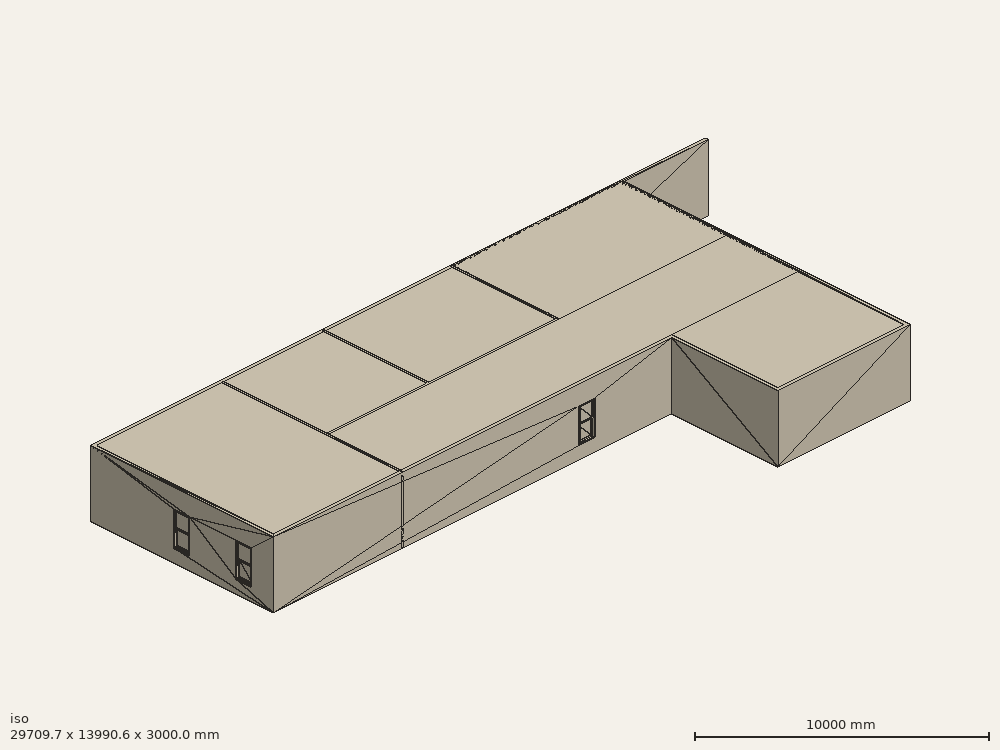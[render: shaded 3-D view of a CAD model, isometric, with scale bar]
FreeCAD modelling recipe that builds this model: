
FCSTD DOCUMENT  (FreeCAD 1.1R39750 (Git))
Label: sm8propc
License: All rights reserved
objects: Part::FeaturePython×23, Sketcher::SketchObject×19, App::DocumentObjectGroup×5, App::GeometryPython×2, Part::Part2DObjectPython×1, App::FeaturePython×1, Spreadsheet::Sheet×1
note: 64 computed .brp shape members not serialized (recipe doc carries the construction recipe); baked Part::Feature solids carry a one-line shape summary decoded from their .brp

FEATURE [Part::Part2DObjectPython] Rectangle  label="Building Outline"  # Draft 2D object (typed FeaturePython)
  Area = 0
  ChamferSize = 0
  Columns = 1
  FilletRadius = 0
  Height = 24384
  Length = 30480
  MakeFace = false
  Rows = 1
FEATURE [App::FeaturePython] Text  label="Building Label"  # WARN: FeaturePython — macro-defined, semantics opaque (R4)
  Placement = pos=(60.96,-290.576,0) rot=(0,0,1;0rad)
  Text =  Building
FEATURE [Sketcher::SketchObject] Sketch
  ArcFitTolerance = 1e-06
  ExternalTypes = [0]
  FullyConstrained = false
  MakeInternals = false
  sketch-geometry (6):
    g0: LineSegment StartX=1970.5 StartY=20576.5 StartZ=0 EndX=27570.1 EndY=20576.5 EndZ=0
    g1: LineSegment StartX=27570.1 StartY=20576.5 StartZ=0 EndX=27570.1 EndY=6625.89 EndZ=0
    g2: LineSegment StartX=27570.1 StartY=6625.89 StartZ=0 EndX=21181.9 EndY=6625.89 EndZ=0
    g3: LineSegment StartX=21181.9 StartY=6625.89 StartZ=0 EndX=21181.9 EndY=11745.8 EndZ=0
    g4: LineSegment StartX=21181.9 StartY=11745.8 StartZ=0 EndX=1970.5 EndY=11745.8 EndZ=0
    g5: LineSegment StartX=1970.5 StartY=11745.8 StartZ=0 EndX=1970.5 EndY=20576.5 EndZ=0
  constraints (12):
    c: Horizontal(g0)
    c: Coincident(g0,g1)
    c: Vertical(g1)
    c: Coincident(g1,g2)
    c: Horizontal(g2)
    c: Coincident(g2,g3)
    c: Vertical(g3)
    c: Coincident(g3,g4)
    c: Horizontal(g4)
    c: Coincident(g4,g5)
    c: Coincident(g5,g0)
    c: Vertical(g5)
FEATURE [App::DocumentObjectGroup] App__DocumentObjectGroup  label="Building Layout"
  Group = -> [Rectangle,Sketch,Text]
FEATURE [App::DocumentObjectGroup] Group001  label="Floors"
FEATURE [Sketcher::SketchObject] Sketch001
  ArcFitTolerance = 1e-06
  ExternalGeometry = -> [Sketch]
  ExternalTypes = [0]
  FullyConstrained = false
  MakeInternals = false
  sketch-geometry (6):
    g0: LineSegment StartX=27570.1 StartY=20576.5 StartZ=0 EndX=27570.1 EndY=6625.89 EndZ=0
    g1: LineSegment StartX=27570.1 StartY=6625.89 StartZ=0 EndX=21181.9 EndY=6625.89 EndZ=0
    g2: LineSegment StartX=21181.9 StartY=6625.89 StartZ=0 EndX=21181.9 EndY=11745.8 EndZ=0
    g3: LineSegment StartX=21181.9 StartY=11745.8 StartZ=0 EndX=1970.5 EndY=11745.8 EndZ=0
    g4: LineSegment StartX=1970.5 StartY=11745.8 StartZ=0 EndX=1970.5 EndY=20576.5 EndZ=0
    g5: LineSegment StartX=1970.5 StartY=20576.5 StartZ=0 EndX=23456.9 EndY=20576.5 EndZ=0
  constraints (10):
    c: Coincident(g0,g-5)
    c: Coincident(g0,g1)
    c: Coincident(g1,g-4)
    c: Coincident(g1,g2)
    c: Coincident(g2,g-4)
    c: Coincident(g2,g3)
    c: Coincident(g3,g-3)
    c: Coincident(g3,g4)
    c: Coincident(g5,g4)
    c: Horizontal(g5)
FEATURE [Part::FeaturePython] Wall  # Arch/BIM 166 (typed FeaturePython)
  Align = 0
  ArchSketchData = true
  ArchSketchPropertySet = 0
  Area = 2.2359e+08
  Base = -> Sketch001
  BlockHeight = 0
  BlockLength = 0
  CountBroken = 0
  CountEntire = 0
  Face = 0
  GlobalId = 2YRsmEokzAbB9aqL5j59_R
  Height = 3000
  HorizontalArea = 0
  IfcData = IfcUID=2YRsmEokzAbB9aqL5j59_R,+2 more (map truncated)
  IfcProperties = AcousticRating;;Pset_WallCommon=IfcLabel;;,Combustible;;Pset_WallCommon=IfcBoolean;;,Compartmentation;;Pset_WallCommon=IfcBoolean;;,+7 more (map truncated)
  IfcType = 166
  Joint = 0
  Length = 74529.9
  MakeBlocks = false
  MoveBase = false
  MoveWithHost = false
  Normal = (0,0,0)
  OffsetFirst = 0
  OffsetSecond = 0
  PerimeterLength = 0
  PredefinedType = 0
  VerticalArea = 0
  Width = 152.4
FEATURE [Sketcher::SketchObject] Sketch002
  ArcFitTolerance = 1e-06
  ExternalGeometry = -> [Sketch]
  ExternalTypes = [0]
  FullyConstrained = false
  MakeInternals = false
  sketch-geometry (6):
    g0: LineSegment StartX=19340.5 StartY=20576.5 StartZ=0 EndX=19340.5 EndY=15418.3 EndZ=0
    g1: LineSegment StartX=19340.5 StartY=15418.3 StartZ=0 EndX=13139 EndY=15418.3 EndZ=0
    g2: LineSegment StartX=13139 StartY=15418.3 StartZ=0 EndX=13139 EndY=20576.5 EndZ=0
    g3: LineSegment StartX=13139 StartY=15418.3 StartZ=0 EndX=8206.95 EndY=15418.3 EndZ=0
    g4: LineSegment StartX=8206.95 StartY=15418.3 StartZ=0 EndX=8206.95 EndY=20576.5 EndZ=0
    g5: LineSegment StartX=8206.95 StartY=15418.3 StartZ=0 EndX=8206.95 EndY=11745.8 EndZ=0
  constraints (16):
    c: PointOnObject(g0,g-3)
    c: Vertical(g0)
    c: Coincident(g0,g1)
    c: Horizontal(g1)
    c: Coincident(g1,g2)
    c: PointOnObject(g2,g-3)
    c: Vertical(g2)
    c: Coincident(g1,g3)
    c: Horizontal(g3)
    c: Coincident(g3,g4)
    c: PointOnObject(g4,g-3)
    c: Vertical(g4)
    c: Coincident(g3,g5)
    c: Vertical(g5)
    c: DistanceY(g5,g-4) = 0
    c: DistanceX(g0,g-3) = 8229.6
FEATURE [Part::FeaturePython] Wall001  # Arch/BIM 166 (typed FeaturePython)
  Align = 2
  ArchSketchData = true
  ArchSketchPropertySet = 0
  Area = 9.08412e+07
  Base = -> Sketch002
  BlockHeight = 0
  BlockLength = 0
  CountBroken = 0
  CountEntire = 0
  Face = 0
  GlobalId = 1JO$GA0_55Qeh9h4$oH2jA
  Height = 3000
  HorizontalArea = 0
  IfcData = IfcUID=1JO$GA0_55Qeh9h4$oH2jA,+2 more (map truncated)
  IfcType = 166
  Joint = 0
  Length = 30280.4
  MakeBlocks = false
  MoveBase = false
  MoveWithHost = false
  Normal = (0,0,0)
  OffsetFirst = 0
  OffsetSecond = 0
  PerimeterLength = 0
  PredefinedType = 0
  VerticalArea = 0
  Width = 101.6
FEATURE [Sketcher::SketchObject] Sketch003
  ArcFitTolerance = 1e-06
  ExternalTypes = [0]
  FullyConstrained = true
  MakeInternals = false
  Placement = pos=(27570.1,8934.96,609.6) rot=(0.57735,0.57735,0.57735;2.0944rad)
  sketch-geometry (24):
    g0: LineSegment StartX=0 StartY=0 StartZ=0 EndX=762 EndY=0 EndZ=0
    g1: LineSegment StartX=762 StartY=0 StartZ=0 EndX=762 EndY=1524 EndZ=0
    g2: LineSegment StartX=762 StartY=1524 StartZ=0 EndX=0 EndY=1524 EndZ=0
    g3: LineSegment StartX=0 StartY=1524 StartZ=0 EndX=0 EndY=0 EndZ=0
    g4: LineSegment StartX=25 StartY=25 StartZ=0 EndX=737 EndY=25 EndZ=0
    g5: LineSegment StartX=737 StartY=25 StartZ=0 EndX=737 EndY=1499 EndZ=0
    g6: LineSegment StartX=737 StartY=1499 StartZ=0 EndX=25 EndY=1499 EndZ=0
    g7: LineSegment StartX=25 StartY=1499 StartZ=0 EndX=25 EndY=25 EndZ=0
    g8: LineSegment StartX=27.5 StartY=27.5 StartZ=0 EndX=734.5 EndY=27.5 EndZ=0
    g9: LineSegment StartX=734.5 StartY=27.5 StartZ=0 EndX=734.5 EndY=760.75 EndZ=0
    g10: LineSegment StartX=734.5 StartY=760.75 StartZ=0 EndX=27.5 EndY=760.75 EndZ=0
    g11: LineSegment StartX=27.5 StartY=760.75 StartZ=0 EndX=27.5 EndY=27.5 EndZ=0
    g12: LineSegment StartX=77.5 StartY=77.5 StartZ=0 EndX=684.5 EndY=77.5 EndZ=0
    g13: LineSegment StartX=684.5 StartY=77.5 StartZ=0 EndX=684.5 EndY=710.75 EndZ=0
    g14: LineSegment StartX=684.5 StartY=710.75 StartZ=0 EndX=77.5 EndY=710.75 EndZ=0
    g15: LineSegment StartX=77.5 StartY=710.75 StartZ=0 EndX=77.5 EndY=77.5 EndZ=0
    g16: LineSegment StartX=27.5 StartY=763.25 StartZ=0 EndX=734.5 EndY=763.25 EndZ=0
    g17: LineSegment StartX=734.5 StartY=763.25 StartZ=0 EndX=734.5 EndY=1496.5 EndZ=0
    g18: LineSegment StartX=734.5 StartY=1496.5 StartZ=0 EndX=27.5 EndY=1496.5 EndZ=0
    g19: LineSegment StartX=27.5 StartY=1496.5 StartZ=0 EndX=27.5 EndY=763.25 EndZ=0
    g20: LineSegment StartX=77.5 StartY=813.25 StartZ=0 EndX=684.5 EndY=813.25 EndZ=0
    g21: LineSegment StartX=684.5 StartY=813.25 StartZ=0 EndX=684.5 EndY=1446.5 EndZ=0
    g22: LineSegment StartX=684.5 StartY=1446.5 StartZ=0 EndX=77.5 EndY=1446.5 EndZ=0
    g23: LineSegment StartX=77.5 StartY=1446.5 StartZ=0 EndX=77.5 EndY=813.25 EndZ=0
  constraints (71):
    c: Coincident(g0,g1)
    c: Coincident(g1,g2)
    c: Coincident(g2,g3)
    c: Coincident(g3,g0)
    c: Horizontal(g0)
    c: Horizontal(g2)
    c: Vertical(g1)
    c: Vertical(g3)
    c: Coincident(g4,g5)
    c: Coincident(g5,g6)
    c: Coincident(g6,g7)
    c: Coincident(g7,g4)
    c: Horizontal(g4)
    c: Horizontal(g6)
    c: Vertical(g5)
    c: Vertical(g7)
    c: DistanceY(g1) = 1524  'Height'
    c: DistanceX(g0) = 762  'Width'
    c: DistanceY(g6,g2) = 25  'Frame1'
    c: DistanceX(g2,g6) = 25  'Frame2'
    c: DistanceX(g4,g0) = 25  'Frame3'
    c: DistanceY(g0,g4) = 25  'Frame4'
    c: Coincident(g0,g-1)
    c: Coincident(g8,g9)
    c: Coincident(g9,g10)
    c: Coincident(g10,g11)
    c: Coincident(g11,g8)
    c: Horizontal(g8)
    c: Horizontal(g10)
    c: Vertical(g9)
    c: Vertical(g11)
    c: Coincident(g12,g13)
    c: Coincident(g13,g14)
    c: Coincident(g14,g15)
    c: Coincident(g15,g12)
    c: Horizontal(g12)
    c: Horizontal(g14)
    c: Vertical(g13)
    c: Vertical(g15)
    c: Coincident(g16,g17)
    c: Coincident(g17,g18)
    c: Coincident(g18,g19)
    c: Coincident(g19,g16)
    c: Horizontal(g16)
    c: Horizontal(g18)
    c: Vertical(g17)
    c: Vertical(g19)
    c: Coincident(g20,g21)
    c: Coincident(g21,g22)
    c: Coincident(g22,g23)
    c: Coincident(g23,g20)
    c: Horizontal(g20)
    c: Horizontal(g22)
    c: Vertical(g21)
    c: Vertical(g23)
    c: DistanceY(g8,g12) = 50
    c: DistanceX(g8,g12) = 50
    c: DistanceX(g21,g17) = 50
    c: DistanceY(g21,g17) = 50
    c: DistanceY(g16,g20) = 50
    c: DistanceY(g10,g14) = -50
    c: Equal(g23,g15)
    c: DistanceX(g12,g20) = 0
    c: DistanceX(g13,g20) = 0
    c: DistanceX(g4,g8) = 2.5
    c: DistanceY(g4,g8) = 2.5
    c: DistanceX(g6,g18) = -2.5
    c: DistanceY(g6,g18) = -2.5
    c: DistanceY(g10,g16) = 2.5
    c: PointOnObject(g9,g17)
    c: PointOnObject(g16,g11)
FEATURE [Part::FeaturePython] Window  # Arch/BIM 170 (typed FeaturePython)
  Area = 1161288
  Base = -> Sketch003
  Frame = 50.8
  GlobalId = 2kA35zzJj5FhV35RYvWuJY
  Height = 1524
  HoleDepth = 0
  HoleWire = 0
  HorizontalArea = 0
  Hosts = -> [Wall]
  IfcData = IfcUID=2kA35zzJj5FhV35RYvWuJY,+2 more (map truncated)
  IfcType = 170
  LouvreSpacing = 0
  LouvreWidth = 0
  MoveBase = false
  MoveWithHost = true
  Normal = (-1,0,0)
  Opening = 0
  OverallHeight = 1524
  OverallWidth = 762
  PartitioningType = 0
  PerimeterLength = 0
  PredefinedType = 0
  Preset = 4
  SymbolElevation = false
  SymbolPlan = false
  VerticalArea = 0
  Width = 762
  WindowParts = OuterFrame | Frame | Wire0,Wire1 | -90.8+V | 0.00+V | LowerFrame | Frame | Wire2,Wire3 | 50.8 | 75.8+V | LowerGlass | Glass panel | Wire3 | 5.08 | 101.19999999999999+V | UpperFrame | Frame | Wire4,Wire5 | 50.8 | 25.0+V | UpperGlass | Glass panel | Wire5 | 5.08 | 50.4+V
  expr: OverallHeight = .Height.Value
  expr: OverallWidth = .Width.Value
FEATURE [Sketcher::SketchObject] Sketch004
  ArcFitTolerance = 1e-06
  ExternalTypes = [0]
  FullyConstrained = true
  MakeInternals = false
  Placement = pos=(27570.1,18031.7,609.6) rot=(0.57735,0.57735,0.57735;2.0944rad)
  sketch-geometry (24):
    g0: LineSegment StartX=0 StartY=0 StartZ=0 EndX=762 EndY=0 EndZ=0
    g1: LineSegment StartX=762 StartY=0 StartZ=0 EndX=762 EndY=1524 EndZ=0
    g2: LineSegment StartX=762 StartY=1524 StartZ=0 EndX=0 EndY=1524 EndZ=0
    g3: LineSegment StartX=0 StartY=1524 StartZ=0 EndX=0 EndY=0 EndZ=0
    g4: LineSegment StartX=25 StartY=25 StartZ=0 EndX=737 EndY=25 EndZ=0
    g5: LineSegment StartX=737 StartY=25 StartZ=0 EndX=737 EndY=1499 EndZ=0
    g6: LineSegment StartX=737 StartY=1499 StartZ=0 EndX=25 EndY=1499 EndZ=0
    g7: LineSegment StartX=25 StartY=1499 StartZ=0 EndX=25 EndY=25 EndZ=0
    g8: LineSegment StartX=27.5 StartY=27.5 StartZ=0 EndX=734.5 EndY=27.5 EndZ=0
    g9: LineSegment StartX=734.5 StartY=27.5 StartZ=0 EndX=734.5 EndY=760.75 EndZ=0
    g10: LineSegment StartX=734.5 StartY=760.75 StartZ=0 EndX=27.5 EndY=760.75 EndZ=0
    g11: LineSegment StartX=27.5 StartY=760.75 StartZ=0 EndX=27.5 EndY=27.5 EndZ=0
    g12: LineSegment StartX=77.5 StartY=77.5 StartZ=0 EndX=684.5 EndY=77.5 EndZ=0
    g13: LineSegment StartX=684.5 StartY=77.5 StartZ=0 EndX=684.5 EndY=710.75 EndZ=0
    g14: LineSegment StartX=684.5 StartY=710.75 StartZ=0 EndX=77.5 EndY=710.75 EndZ=0
    g15: LineSegment StartX=77.5 StartY=710.75 StartZ=0 EndX=77.5 EndY=77.5 EndZ=0
    g16: LineSegment StartX=27.5 StartY=763.25 StartZ=0 EndX=734.5 EndY=763.25 EndZ=0
    g17: LineSegment StartX=734.5 StartY=763.25 StartZ=0 EndX=734.5 EndY=1496.5 EndZ=0
    g18: LineSegment StartX=734.5 StartY=1496.5 StartZ=0 EndX=27.5 EndY=1496.5 EndZ=0
    g19: LineSegment StartX=27.5 StartY=1496.5 StartZ=0 EndX=27.5 EndY=763.25 EndZ=0
    g20: LineSegment StartX=77.5 StartY=813.25 StartZ=0 EndX=684.5 EndY=813.25 EndZ=0
    g21: LineSegment StartX=684.5 StartY=813.25 StartZ=0 EndX=684.5 EndY=1446.5 EndZ=0
    g22: LineSegment StartX=684.5 StartY=1446.5 StartZ=0 EndX=77.5 EndY=1446.5 EndZ=0
    g23: LineSegment StartX=77.5 StartY=1446.5 StartZ=0 EndX=77.5 EndY=813.25 EndZ=0
  constraints (71):
    c: Coincident(g0,g1)
    c: Coincident(g1,g2)
    c: Coincident(g2,g3)
    c: Coincident(g3,g0)
    c: Horizontal(g0)
    c: Horizontal(g2)
    c: Vertical(g1)
    c: Vertical(g3)
    c: Coincident(g4,g5)
    c: Coincident(g5,g6)
    c: Coincident(g6,g7)
    c: Coincident(g7,g4)
    c: Horizontal(g4)
    c: Horizontal(g6)
    c: Vertical(g5)
    c: Vertical(g7)
    c: DistanceY(g1) = 1524  'Height'
    c: DistanceX(g0) = 762  'Width'
    c: DistanceY(g6,g2) = 25  'Frame1'
    c: DistanceX(g2,g6) = 25  'Frame2'
    c: DistanceX(g4,g0) = 25  'Frame3'
    c: DistanceY(g0,g4) = 25  'Frame4'
    c: Coincident(g0,g-1)
    c: Coincident(g8,g9)
    c: Coincident(g9,g10)
    c: Coincident(g10,g11)
    c: Coincident(g11,g8)
    c: Horizontal(g8)
    c: Horizontal(g10)
    c: Vertical(g9)
    c: Vertical(g11)
    c: Coincident(g12,g13)
    c: Coincident(g13,g14)
    c: Coincident(g14,g15)
    c: Coincident(g15,g12)
    c: Horizontal(g12)
    c: Horizontal(g14)
    c: Vertical(g13)
    c: Vertical(g15)
    c: Coincident(g16,g17)
    c: Coincident(g17,g18)
    c: Coincident(g18,g19)
    c: Coincident(g19,g16)
    c: Horizontal(g16)
    c: Horizontal(g18)
    c: Vertical(g17)
    c: Vertical(g19)
    c: Coincident(g20,g21)
    c: Coincident(g21,g22)
    c: Coincident(g22,g23)
    c: Coincident(g23,g20)
    c: Horizontal(g20)
    c: Horizontal(g22)
    c: Vertical(g21)
    c: Vertical(g23)
    c: DistanceY(g8,g12) = 50
    c: DistanceX(g8,g12) = 50
    c: DistanceX(g21,g17) = 50
    c: DistanceY(g21,g17) = 50
    c: DistanceY(g16,g20) = 50
    c: DistanceY(g10,g14) = -50
    c: Equal(g23,g15)
    c: DistanceX(g12,g20) = 0
    c: DistanceX(g13,g20) = 0
    c: DistanceX(g4,g8) = 2.5
    c: DistanceY(g4,g8) = 2.5
    c: DistanceX(g6,g18) = -2.5
    c: DistanceY(g6,g18) = -2.5
    c: DistanceY(g10,g16) = 2.5
    c: PointOnObject(g9,g17)
    c: PointOnObject(g16,g11)
FEATURE [Part::FeaturePython] Window001  # Arch/BIM 170 (typed FeaturePython)
  Area = 1161288
  Base = -> Sketch004
  Frame = 50.8
  GlobalId = 0Gm0yBXcz24Rl4COUdGdtV
  Height = 1524
  HoleDepth = 0
  HoleWire = 0
  HorizontalArea = 0
  Hosts = -> [Wall]
  IfcData = IfcUID=0Gm0yBXcz24Rl4COUdGdtV,+2 more (map truncated)
  IfcType = 170
  LouvreSpacing = 0
  LouvreWidth = 0
  MoveBase = false
  MoveWithHost = true
  Normal = (-1,0,0)
  Opening = 0
  OverallHeight = 1524
  OverallWidth = 762
  PartitioningType = 0
  PerimeterLength = 0
  PredefinedType = 0
  Preset = 4
  SymbolElevation = false
  SymbolPlan = false
  VerticalArea = 0
  Width = 762
  WindowParts = <same value as first occurrence — deduplicated (x10 in doc)>
  expr: OverallHeight = .Height.Value
  expr: OverallWidth = .Width.Value
FEATURE [Sketcher::SketchObject] Sketch005
  ArcFitTolerance = 1e-06
  ExternalTypes = [0]
  FullyConstrained = true
  MakeInternals = false
  Placement = pos=(21499.9,20576.5,611.457) rot=(0,0.707107,0.707107;3.14159rad)
  sketch-geometry (24):
    g0: LineSegment StartX=0 StartY=0 StartZ=0 EndX=762 EndY=0 EndZ=0
    g1: LineSegment StartX=762 StartY=0 StartZ=0 EndX=762 EndY=1524 EndZ=0
    g2: LineSegment StartX=762 StartY=1524 StartZ=0 EndX=0 EndY=1524 EndZ=0
    g3: LineSegment StartX=0 StartY=1524 StartZ=0 EndX=0 EndY=0 EndZ=0
    g4: LineSegment StartX=25 StartY=25 StartZ=0 EndX=737 EndY=25 EndZ=0
    g5: LineSegment StartX=737 StartY=25 StartZ=0 EndX=737 EndY=1499 EndZ=0
    g6: LineSegment StartX=737 StartY=1499 StartZ=0 EndX=25 EndY=1499 EndZ=0
    g7: LineSegment StartX=25 StartY=1499 StartZ=0 EndX=25 EndY=25 EndZ=0
    g8: LineSegment StartX=27.5 StartY=27.5 StartZ=0 EndX=734.5 EndY=27.5 EndZ=0
    g9: LineSegment StartX=734.5 StartY=27.5 StartZ=0 EndX=734.5 EndY=760.75 EndZ=0
    g10: LineSegment StartX=734.5 StartY=760.75 StartZ=0 EndX=27.5 EndY=760.75 EndZ=0
    g11: LineSegment StartX=27.5 StartY=760.75 StartZ=0 EndX=27.5 EndY=27.5 EndZ=0
    g12: LineSegment StartX=77.5 StartY=77.5 StartZ=0 EndX=684.5 EndY=77.5 EndZ=0
    g13: LineSegment StartX=684.5 StartY=77.5 StartZ=0 EndX=684.5 EndY=710.75 EndZ=0
    g14: LineSegment StartX=684.5 StartY=710.75 StartZ=0 EndX=77.5 EndY=710.75 EndZ=0
    g15: LineSegment StartX=77.5 StartY=710.75 StartZ=0 EndX=77.5 EndY=77.5 EndZ=0
    g16: LineSegment StartX=27.5 StartY=763.25 StartZ=0 EndX=734.5 EndY=763.25 EndZ=0
    g17: LineSegment StartX=734.5 StartY=763.25 StartZ=0 EndX=734.5 EndY=1496.5 EndZ=0
    g18: LineSegment StartX=734.5 StartY=1496.5 StartZ=0 EndX=27.5 EndY=1496.5 EndZ=0
    g19: LineSegment StartX=27.5 StartY=1496.5 StartZ=0 EndX=27.5 EndY=763.25 EndZ=0
    g20: LineSegment StartX=77.5 StartY=813.25 StartZ=0 EndX=684.5 EndY=813.25 EndZ=0
    g21: LineSegment StartX=684.5 StartY=813.25 StartZ=0 EndX=684.5 EndY=1446.5 EndZ=0
    g22: LineSegment StartX=684.5 StartY=1446.5 StartZ=0 EndX=77.5 EndY=1446.5 EndZ=0
    g23: LineSegment StartX=77.5 StartY=1446.5 StartZ=0 EndX=77.5 EndY=813.25 EndZ=0
  constraints (71):
    c: Coincident(g0,g1)
    c: Coincident(g1,g2)
    c: Coincident(g2,g3)
    c: Coincident(g3,g0)
    c: Horizontal(g0)
    c: Horizontal(g2)
    c: Vertical(g1)
    c: Vertical(g3)
    c: Coincident(g4,g5)
    c: Coincident(g5,g6)
    c: Coincident(g6,g7)
    c: Coincident(g7,g4)
    c: Horizontal(g4)
    c: Horizontal(g6)
    c: Vertical(g5)
    c: Vertical(g7)
    c: DistanceY(g1) = 1524  'Height'
    c: DistanceX(g0) = 762  'Width'
    c: DistanceY(g6,g2) = 25  'Frame1'
    c: DistanceX(g2,g6) = 25  'Frame2'
    c: DistanceX(g4,g0) = 25  'Frame3'
    c: DistanceY(g0,g4) = 25  'Frame4'
    c: Coincident(g0,g-1)
    c: Coincident(g8,g9)
    c: Coincident(g9,g10)
    c: Coincident(g10,g11)
    c: Coincident(g11,g8)
    c: Horizontal(g8)
    c: Horizontal(g10)
    c: Vertical(g9)
    c: Vertical(g11)
    c: Coincident(g12,g13)
    c: Coincident(g13,g14)
    c: Coincident(g14,g15)
    c: Coincident(g15,g12)
    c: Horizontal(g12)
    c: Horizontal(g14)
    c: Vertical(g13)
    c: Vertical(g15)
    c: Coincident(g16,g17)
    c: Coincident(g17,g18)
    c: Coincident(g18,g19)
    c: Coincident(g19,g16)
    c: Horizontal(g16)
    c: Horizontal(g18)
    c: Vertical(g17)
    c: Vertical(g19)
    c: Coincident(g20,g21)
    c: Coincident(g21,g22)
    c: Coincident(g22,g23)
    c: Coincident(g23,g20)
    c: Horizontal(g20)
    c: Horizontal(g22)
    c: Vertical(g21)
    c: Vertical(g23)
    c: DistanceY(g8,g12) = 50
    c: DistanceX(g8,g12) = 50
    c: DistanceX(g21,g17) = 50
    c: DistanceY(g21,g17) = 50
    c: DistanceY(g16,g20) = 50
    c: DistanceY(g10,g14) = -50
    c: Equal(g23,g15)
    c: DistanceX(g12,g20) = 0
    c: DistanceX(g13,g20) = 0
    c: DistanceX(g4,g8) = 2.5
    c: DistanceY(g4,g8) = 2.5
    c: DistanceX(g6,g18) = -2.5
    c: DistanceY(g6,g18) = -2.5
    c: DistanceY(g10,g16) = 2.5
    c: PointOnObject(g9,g17)
    c: PointOnObject(g16,g11)
FEATURE [Part::FeaturePython] Window002  # Arch/BIM 170 (typed FeaturePython)
  Area = 1161288
  Base = -> Sketch005
  Frame = 50.8
  GlobalId = 1_nrbuonLC$gQXA2knc8Ya
  Height = 1524
  HoleDepth = 0
  HoleWire = 0
  HorizontalArea = 0
  Hosts = -> [Wall]
  IfcData = IfcUID=1_nrbuonLC$gQXA2knc8Ya,+2 more (map truncated)
  IfcType = 170
  LouvreSpacing = 0
  LouvreWidth = 0
  MoveBase = false
  MoveWithHost = true
  Normal = (0,-1,2e-16)
  Opening = 0
  OverallHeight = 1524
  OverallWidth = 762
  PartitioningType = 0
  PerimeterLength = 0
  PredefinedType = 0
  Preset = 4
  SymbolElevation = false
  SymbolPlan = false
  VerticalArea = 0
  Width = 762
  WindowParts = <same value as first occurrence — deduplicated (x10 in doc)>
  expr: OverallHeight = .Height.Value
  expr: OverallWidth = .Width.Value
FEATURE [Sketcher::SketchObject] Sketch006
  ArcFitTolerance = 1e-06
  ExternalTypes = [0]
  FullyConstrained = true
  MakeInternals = false
  Placement = pos=(17406.2,20576.5,609.6) rot=(0,0.707107,0.707107;3.14159rad)
  sketch-geometry (24):
    g0: LineSegment StartX=0 StartY=0 StartZ=0 EndX=762 EndY=0 EndZ=0
    g1: LineSegment StartX=762 StartY=0 StartZ=0 EndX=762 EndY=1524 EndZ=0
    g2: LineSegment StartX=762 StartY=1524 StartZ=0 EndX=0 EndY=1524 EndZ=0
    g3: LineSegment StartX=0 StartY=1524 StartZ=0 EndX=0 EndY=0 EndZ=0
    g4: LineSegment StartX=25 StartY=25 StartZ=0 EndX=737 EndY=25 EndZ=0
    g5: LineSegment StartX=737 StartY=25 StartZ=0 EndX=737 EndY=1499 EndZ=0
    g6: LineSegment StartX=737 StartY=1499 StartZ=0 EndX=25 EndY=1499 EndZ=0
    g7: LineSegment StartX=25 StartY=1499 StartZ=0 EndX=25 EndY=25 EndZ=0
    g8: LineSegment StartX=27.5 StartY=27.5 StartZ=0 EndX=734.5 EndY=27.5 EndZ=0
    g9: LineSegment StartX=734.5 StartY=27.5 StartZ=0 EndX=734.5 EndY=760.75 EndZ=0
    g10: LineSegment StartX=734.5 StartY=760.75 StartZ=0 EndX=27.5 EndY=760.75 EndZ=0
    g11: LineSegment StartX=27.5 StartY=760.75 StartZ=0 EndX=27.5 EndY=27.5 EndZ=0
    g12: LineSegment StartX=77.5 StartY=77.5 StartZ=0 EndX=684.5 EndY=77.5 EndZ=0
    g13: LineSegment StartX=684.5 StartY=77.5 StartZ=0 EndX=684.5 EndY=710.75 EndZ=0
    g14: LineSegment StartX=684.5 StartY=710.75 StartZ=0 EndX=77.5 EndY=710.75 EndZ=0
    g15: LineSegment StartX=77.5 StartY=710.75 StartZ=0 EndX=77.5 EndY=77.5 EndZ=0
    g16: LineSegment StartX=27.5 StartY=763.25 StartZ=0 EndX=734.5 EndY=763.25 EndZ=0
    g17: LineSegment StartX=734.5 StartY=763.25 StartZ=0 EndX=734.5 EndY=1496.5 EndZ=0
    g18: LineSegment StartX=734.5 StartY=1496.5 StartZ=0 EndX=27.5 EndY=1496.5 EndZ=0
    g19: LineSegment StartX=27.5 StartY=1496.5 StartZ=0 EndX=27.5 EndY=763.25 EndZ=0
    g20: LineSegment StartX=77.5 StartY=813.25 StartZ=0 EndX=684.5 EndY=813.25 EndZ=0
    g21: LineSegment StartX=684.5 StartY=813.25 StartZ=0 EndX=684.5 EndY=1446.5 EndZ=0
    g22: LineSegment StartX=684.5 StartY=1446.5 StartZ=0 EndX=77.5 EndY=1446.5 EndZ=0
    g23: LineSegment StartX=77.5 StartY=1446.5 StartZ=0 EndX=77.5 EndY=813.25 EndZ=0
  constraints (71):
    c: Coincident(g0,g1)
    c: Coincident(g1,g2)
    c: Coincident(g2,g3)
    c: Coincident(g3,g0)
    c: Horizontal(g0)
    c: Horizontal(g2)
    c: Vertical(g1)
    c: Vertical(g3)
    c: Coincident(g4,g5)
    c: Coincident(g5,g6)
    c: Coincident(g6,g7)
    c: Coincident(g7,g4)
    c: Horizontal(g4)
    c: Horizontal(g6)
    c: Vertical(g5)
    c: Vertical(g7)
    c: DistanceY(g1) = 1524  'Height'
    c: DistanceX(g0) = 762  'Width'
    c: DistanceY(g6,g2) = 25  'Frame1'
    c: DistanceX(g2,g6) = 25  'Frame2'
    c: DistanceX(g4,g0) = 25  'Frame3'
    c: DistanceY(g0,g4) = 25  'Frame4'
    c: Coincident(g0,g-1)
    c: Coincident(g8,g9)
    c: Coincident(g9,g10)
    c: Coincident(g10,g11)
    c: Coincident(g11,g8)
    c: Horizontal(g8)
    c: Horizontal(g10)
    c: Vertical(g9)
    c: Vertical(g11)
    c: Coincident(g12,g13)
    c: Coincident(g13,g14)
    c: Coincident(g14,g15)
    c: Coincident(g15,g12)
    c: Horizontal(g12)
    c: Horizontal(g14)
    c: Vertical(g13)
    c: Vertical(g15)
    c: Coincident(g16,g17)
    c: Coincident(g17,g18)
    c: Coincident(g18,g19)
    c: Coincident(g19,g16)
    c: Horizontal(g16)
    c: Horizontal(g18)
    c: Vertical(g17)
    c: Vertical(g19)
    c: Coincident(g20,g21)
    c: Coincident(g21,g22)
    c: Coincident(g22,g23)
    c: Coincident(g23,g20)
    c: Horizontal(g20)
    c: Horizontal(g22)
    c: Vertical(g21)
    c: Vertical(g23)
    c: DistanceY(g8,g12) = 50
    c: DistanceX(g8,g12) = 50
    c: DistanceX(g21,g17) = 50
    c: DistanceY(g21,g17) = 50
    c: DistanceY(g16,g20) = 50
    c: DistanceY(g10,g14) = -50
    c: Equal(g23,g15)
    c: DistanceX(g12,g20) = 0
    c: DistanceX(g13,g20) = 0
    c: DistanceX(g4,g8) = 2.5
    c: DistanceY(g4,g8) = 2.5
    c: DistanceX(g6,g18) = -2.5
    c: DistanceY(g6,g18) = -2.5
    c: DistanceY(g10,g16) = 2.5
    c: PointOnObject(g9,g17)
    c: PointOnObject(g16,g11)
FEATURE [Part::FeaturePython] Window003  # Arch/BIM 170 (typed FeaturePython)
  Area = 1161288
  Base = -> Sketch006
  Frame = 50.8
  GlobalId = 0bJBue1qL8l8j0EzGdZafv
  Height = 1524
  HoleDepth = 0
  HoleWire = 0
  HorizontalArea = 0
  Hosts = -> [Wall]
  IfcData = IfcUID=0bJBue1qL8l8j0EzGdZafv,+2 more (map truncated)
  IfcType = 170
  LouvreSpacing = 0
  LouvreWidth = 0
  MoveBase = false
  MoveWithHost = true
  Normal = (0,-1,2e-16)
  Opening = 0
  OverallHeight = 1524
  OverallWidth = 762
  PartitioningType = 0
  PerimeterLength = 0
  PredefinedType = 0
  Preset = 4
  SymbolElevation = false
  SymbolPlan = false
  VerticalArea = 0
  Width = 762
  WindowParts = <same value as first occurrence — deduplicated (x10 in doc)>
  expr: OverallHeight = .Height.Value
  expr: OverallWidth = .Width.Value
FEATURE [Sketcher::SketchObject] Sketch007
  ArcFitTolerance = 1e-06
  ExternalTypes = [0]
  FullyConstrained = true
  MakeInternals = false
  Placement = pos=(11820.4,20576.5,609.6) rot=(0,0.707107,0.707107;3.14159rad)
  sketch-geometry (24):
    g0: LineSegment StartX=0 StartY=0 StartZ=0 EndX=762 EndY=0 EndZ=0
    g1: LineSegment StartX=762 StartY=0 StartZ=0 EndX=762 EndY=1524 EndZ=0
    g2: LineSegment StartX=762 StartY=1524 StartZ=0 EndX=0 EndY=1524 EndZ=0
    g3: LineSegment StartX=0 StartY=1524 StartZ=0 EndX=0 EndY=0 EndZ=0
    g4: LineSegment StartX=25 StartY=25 StartZ=0 EndX=737 EndY=25 EndZ=0
    g5: LineSegment StartX=737 StartY=25 StartZ=0 EndX=737 EndY=1499 EndZ=0
    g6: LineSegment StartX=737 StartY=1499 StartZ=0 EndX=25 EndY=1499 EndZ=0
    g7: LineSegment StartX=25 StartY=1499 StartZ=0 EndX=25 EndY=25 EndZ=0
    g8: LineSegment StartX=27.5 StartY=27.5 StartZ=0 EndX=734.5 EndY=27.5 EndZ=0
    g9: LineSegment StartX=734.5 StartY=27.5 StartZ=0 EndX=734.5 EndY=760.75 EndZ=0
    g10: LineSegment StartX=734.5 StartY=760.75 StartZ=0 EndX=27.5 EndY=760.75 EndZ=0
    g11: LineSegment StartX=27.5 StartY=760.75 StartZ=0 EndX=27.5 EndY=27.5 EndZ=0
    g12: LineSegment StartX=77.5 StartY=77.5 StartZ=0 EndX=684.5 EndY=77.5 EndZ=0
    g13: LineSegment StartX=684.5 StartY=77.5 StartZ=0 EndX=684.5 EndY=710.75 EndZ=0
    g14: LineSegment StartX=684.5 StartY=710.75 StartZ=0 EndX=77.5 EndY=710.75 EndZ=0
    g15: LineSegment StartX=77.5 StartY=710.75 StartZ=0 EndX=77.5 EndY=77.5 EndZ=0
    g16: LineSegment StartX=27.5 StartY=763.25 StartZ=0 EndX=734.5 EndY=763.25 EndZ=0
    g17: LineSegment StartX=734.5 StartY=763.25 StartZ=0 EndX=734.5 EndY=1496.5 EndZ=0
    g18: LineSegment StartX=734.5 StartY=1496.5 StartZ=0 EndX=27.5 EndY=1496.5 EndZ=0
    g19: LineSegment StartX=27.5 StartY=1496.5 StartZ=0 EndX=27.5 EndY=763.25 EndZ=0
    g20: LineSegment StartX=77.5 StartY=813.25 StartZ=0 EndX=684.5 EndY=813.25 EndZ=0
    g21: LineSegment StartX=684.5 StartY=813.25 StartZ=0 EndX=684.5 EndY=1446.5 EndZ=0
    g22: LineSegment StartX=684.5 StartY=1446.5 StartZ=0 EndX=77.5 EndY=1446.5 EndZ=0
    g23: LineSegment StartX=77.5 StartY=1446.5 StartZ=0 EndX=77.5 EndY=813.25 EndZ=0
  constraints (71):
    c: Coincident(g0,g1)
    c: Coincident(g1,g2)
    c: Coincident(g2,g3)
    c: Coincident(g3,g0)
    c: Horizontal(g0)
    c: Horizontal(g2)
    c: Vertical(g1)
    c: Vertical(g3)
    c: Coincident(g4,g5)
    c: Coincident(g5,g6)
    c: Coincident(g6,g7)
    c: Coincident(g7,g4)
    c: Horizontal(g4)
    c: Horizontal(g6)
    c: Vertical(g5)
    c: Vertical(g7)
    c: DistanceY(g1) = 1524  'Height'
    c: DistanceX(g0) = 762  'Width'
    c: DistanceY(g6,g2) = 25  'Frame1'
    c: DistanceX(g2,g6) = 25  'Frame2'
    c: DistanceX(g4,g0) = 25  'Frame3'
    c: DistanceY(g0,g4) = 25  'Frame4'
    c: Coincident(g0,g-1)
    c: Coincident(g8,g9)
    c: Coincident(g9,g10)
    c: Coincident(g10,g11)
    c: Coincident(g11,g8)
    c: Horizontal(g8)
    c: Horizontal(g10)
    c: Vertical(g9)
    c: Vertical(g11)
    c: Coincident(g12,g13)
    c: Coincident(g13,g14)
    c: Coincident(g14,g15)
    c: Coincident(g15,g12)
    c: Horizontal(g12)
    c: Horizontal(g14)
    c: Vertical(g13)
    c: Vertical(g15)
    c: Coincident(g16,g17)
    c: Coincident(g17,g18)
    c: Coincident(g18,g19)
    c: Coincident(g19,g16)
    c: Horizontal(g16)
    c: Horizontal(g18)
    c: Vertical(g17)
    c: Vertical(g19)
    c: Coincident(g20,g21)
    c: Coincident(g21,g22)
    c: Coincident(g22,g23)
    c: Coincident(g23,g20)
    c: Horizontal(g20)
    c: Horizontal(g22)
    c: Vertical(g21)
    c: Vertical(g23)
    c: DistanceY(g8,g12) = 50
    c: DistanceX(g8,g12) = 50
    c: DistanceX(g21,g17) = 50
    c: DistanceY(g21,g17) = 50
    c: DistanceY(g16,g20) = 50
    c: DistanceY(g10,g14) = -50
    c: Equal(g23,g15)
    c: DistanceX(g12,g20) = 0
    c: DistanceX(g13,g20) = 0
    c: DistanceX(g4,g8) = 2.5
    c: DistanceY(g4,g8) = 2.5
    c: DistanceX(g6,g18) = -2.5
    c: DistanceY(g6,g18) = -2.5
    c: DistanceY(g10,g16) = 2.5
    c: PointOnObject(g9,g17)
    c: PointOnObject(g16,g11)
FEATURE [Sketcher::SketchObject] Sketch008
  ArcFitTolerance = 1e-06
  ExternalTypes = [0]
  FullyConstrained = true
  MakeInternals = false
  Placement = pos=(4976.2,20576.5,609.6) rot=(0,0.707107,0.707107;3.14159rad)
  sketch-geometry (24):
    g0: LineSegment StartX=0 StartY=0 StartZ=0 EndX=762 EndY=0 EndZ=0
    g1: LineSegment StartX=762 StartY=0 StartZ=0 EndX=762 EndY=1524 EndZ=0
    g2: LineSegment StartX=762 StartY=1524 StartZ=0 EndX=0 EndY=1524 EndZ=0
    g3: LineSegment StartX=0 StartY=1524 StartZ=0 EndX=0 EndY=0 EndZ=0
    g4: LineSegment StartX=25 StartY=25 StartZ=0 EndX=737 EndY=25 EndZ=0
    g5: LineSegment StartX=737 StartY=25 StartZ=0 EndX=737 EndY=1499 EndZ=0
    g6: LineSegment StartX=737 StartY=1499 StartZ=0 EndX=25 EndY=1499 EndZ=0
    g7: LineSegment StartX=25 StartY=1499 StartZ=0 EndX=25 EndY=25 EndZ=0
    g8: LineSegment StartX=27.5 StartY=27.5 StartZ=0 EndX=734.5 EndY=27.5 EndZ=0
    g9: LineSegment StartX=734.5 StartY=27.5 StartZ=0 EndX=734.5 EndY=760.75 EndZ=0
    g10: LineSegment StartX=734.5 StartY=760.75 StartZ=0 EndX=27.5 EndY=760.75 EndZ=0
    g11: LineSegment StartX=27.5 StartY=760.75 StartZ=0 EndX=27.5 EndY=27.5 EndZ=0
    g12: LineSegment StartX=77.5 StartY=77.5 StartZ=0 EndX=684.5 EndY=77.5 EndZ=0
    g13: LineSegment StartX=684.5 StartY=77.5 StartZ=0 EndX=684.5 EndY=710.75 EndZ=0
    g14: LineSegment StartX=684.5 StartY=710.75 StartZ=0 EndX=77.5 EndY=710.75 EndZ=0
    g15: LineSegment StartX=77.5 StartY=710.75 StartZ=0 EndX=77.5 EndY=77.5 EndZ=0
    g16: LineSegment StartX=27.5 StartY=763.25 StartZ=0 EndX=734.5 EndY=763.25 EndZ=0
    g17: LineSegment StartX=734.5 StartY=763.25 StartZ=0 EndX=734.5 EndY=1496.5 EndZ=0
    g18: LineSegment StartX=734.5 StartY=1496.5 StartZ=0 EndX=27.5 EndY=1496.5 EndZ=0
    g19: LineSegment StartX=27.5 StartY=1496.5 StartZ=0 EndX=27.5 EndY=763.25 EndZ=0
    g20: LineSegment StartX=77.5 StartY=813.25 StartZ=0 EndX=684.5 EndY=813.25 EndZ=0
    g21: LineSegment StartX=684.5 StartY=813.25 StartZ=0 EndX=684.5 EndY=1446.5 EndZ=0
    g22: LineSegment StartX=684.5 StartY=1446.5 StartZ=0 EndX=77.5 EndY=1446.5 EndZ=0
    g23: LineSegment StartX=77.5 StartY=1446.5 StartZ=0 EndX=77.5 EndY=813.25 EndZ=0
  constraints (71):
    c: Coincident(g0,g1)
    c: Coincident(g1,g2)
    c: Coincident(g2,g3)
    c: Coincident(g3,g0)
    c: Horizontal(g0)
    c: Horizontal(g2)
    c: Vertical(g1)
    c: Vertical(g3)
    c: Coincident(g4,g5)
    c: Coincident(g5,g6)
    c: Coincident(g6,g7)
    c: Coincident(g7,g4)
    c: Horizontal(g4)
    c: Horizontal(g6)
    c: Vertical(g5)
    c: Vertical(g7)
    c: DistanceY(g1) = 1524  'Height'
    c: DistanceX(g0) = 762  'Width'
    c: DistanceY(g6,g2) = 25  'Frame1'
    c: DistanceX(g2,g6) = 25  'Frame2'
    c: DistanceX(g4,g0) = 25  'Frame3'
    c: DistanceY(g0,g4) = 25  'Frame4'
    c: Coincident(g0,g-1)
    c: Coincident(g8,g9)
    c: Coincident(g9,g10)
    c: Coincident(g10,g11)
    c: Coincident(g11,g8)
    c: Horizontal(g8)
    c: Horizontal(g10)
    c: Vertical(g9)
    c: Vertical(g11)
    c: Coincident(g12,g13)
    c: Coincident(g13,g14)
    c: Coincident(g14,g15)
    c: Coincident(g15,g12)
    c: Horizontal(g12)
    c: Horizontal(g14)
    c: Vertical(g13)
    c: Vertical(g15)
    c: Coincident(g16,g17)
    c: Coincident(g17,g18)
    c: Coincident(g18,g19)
    c: Coincident(g19,g16)
    c: Horizontal(g16)
    c: Horizontal(g18)
    c: Vertical(g17)
    c: Vertical(g19)
    c: Coincident(g20,g21)
    c: Coincident(g21,g22)
    c: Coincident(g22,g23)
    c: Coincident(g23,g20)
    c: Horizontal(g20)
    c: Horizontal(g22)
    c: Vertical(g21)
    c: Vertical(g23)
    c: DistanceY(g8,g12) = 50
    c: DistanceX(g8,g12) = 50
    c: DistanceX(g21,g17) = 50
    c: DistanceY(g21,g17) = 50
    c: DistanceY(g16,g20) = 50
    c: DistanceY(g10,g14) = -50
    c: Equal(g23,g15)
    c: DistanceX(g12,g20) = 0
    c: DistanceX(g13,g20) = 0
    c: DistanceX(g4,g8) = 2.5
    c: DistanceY(g4,g8) = 2.5
    c: DistanceX(g6,g18) = -2.5
    c: DistanceY(g6,g18) = -2.5
    c: DistanceY(g10,g16) = 2.5
    c: PointOnObject(g9,g17)
    c: PointOnObject(g16,g11)
FEATURE [Sketcher::SketchObject] Sketch009
  ArcFitTolerance = 1e-06
  ExternalTypes = [0]
  FullyConstrained = true
  MakeInternals = false
  Placement = pos=(1970.5,16550.3,609.6) rot=(0.57735,-0.57735,-0.57735;2.0944rad)
  sketch-geometry (24):
    g0: LineSegment StartX=0 StartY=0 StartZ=0 EndX=762 EndY=0 EndZ=0
    g1: LineSegment StartX=762 StartY=0 StartZ=0 EndX=762 EndY=1524 EndZ=0
    g2: LineSegment StartX=762 StartY=1524 StartZ=0 EndX=0 EndY=1524 EndZ=0
    g3: LineSegment StartX=0 StartY=1524 StartZ=0 EndX=0 EndY=0 EndZ=0
    g4: LineSegment StartX=25 StartY=25 StartZ=0 EndX=737 EndY=25 EndZ=0
    g5: LineSegment StartX=737 StartY=25 StartZ=0 EndX=737 EndY=1499 EndZ=0
    g6: LineSegment StartX=737 StartY=1499 StartZ=0 EndX=25 EndY=1499 EndZ=0
    g7: LineSegment StartX=25 StartY=1499 StartZ=0 EndX=25 EndY=25 EndZ=0
    g8: LineSegment StartX=27.5 StartY=27.5 StartZ=0 EndX=734.5 EndY=27.5 EndZ=0
    g9: LineSegment StartX=734.5 StartY=27.5 StartZ=0 EndX=734.5 EndY=760.75 EndZ=0
    g10: LineSegment StartX=734.5 StartY=760.75 StartZ=0 EndX=27.5 EndY=760.75 EndZ=0
    g11: LineSegment StartX=27.5 StartY=760.75 StartZ=0 EndX=27.5 EndY=27.5 EndZ=0
    g12: LineSegment StartX=77.5 StartY=77.5 StartZ=0 EndX=684.5 EndY=77.5 EndZ=0
    g13: LineSegment StartX=684.5 StartY=77.5 StartZ=0 EndX=684.5 EndY=710.75 EndZ=0
    g14: LineSegment StartX=684.5 StartY=710.75 StartZ=0 EndX=77.5 EndY=710.75 EndZ=0
    g15: LineSegment StartX=77.5 StartY=710.75 StartZ=0 EndX=77.5 EndY=77.5 EndZ=0
    g16: LineSegment StartX=27.5 StartY=763.25 StartZ=0 EndX=734.5 EndY=763.25 EndZ=0
    g17: LineSegment StartX=734.5 StartY=763.25 StartZ=0 EndX=734.5 EndY=1496.5 EndZ=0
    g18: LineSegment StartX=734.5 StartY=1496.5 StartZ=0 EndX=27.5 EndY=1496.5 EndZ=0
    g19: LineSegment StartX=27.5 StartY=1496.5 StartZ=0 EndX=27.5 EndY=763.25 EndZ=0
    g20: LineSegment StartX=77.5 StartY=813.25 StartZ=0 EndX=684.5 EndY=813.25 EndZ=0
    g21: LineSegment StartX=684.5 StartY=813.25 StartZ=0 EndX=684.5 EndY=1446.5 EndZ=0
    g22: LineSegment StartX=684.5 StartY=1446.5 StartZ=0 EndX=77.5 EndY=1446.5 EndZ=0
    g23: LineSegment StartX=77.5 StartY=1446.5 StartZ=0 EndX=77.5 EndY=813.25 EndZ=0
  constraints (71):
    c: Coincident(g0,g1)
    c: Coincident(g1,g2)
    c: Coincident(g2,g3)
    c: Coincident(g3,g0)
    c: Horizontal(g0)
    c: Horizontal(g2)
    c: Vertical(g1)
    c: Vertical(g3)
    c: Coincident(g4,g5)
    c: Coincident(g5,g6)
    c: Coincident(g6,g7)
    c: Coincident(g7,g4)
    c: Horizontal(g4)
    c: Horizontal(g6)
    c: Vertical(g5)
    c: Vertical(g7)
    c: DistanceY(g1) = 1524  'Height'
    c: DistanceX(g0) = 762  'Width'
    c: DistanceY(g6,g2) = 25  'Frame1'
    c: DistanceX(g2,g6) = 25  'Frame2'
    c: DistanceX(g4,g0) = 25  'Frame3'
    c: DistanceY(g0,g4) = 25  'Frame4'
    c: Coincident(g0,g-1)
    c: Coincident(g8,g9)
    c: Coincident(g9,g10)
    c: Coincident(g10,g11)
    c: Coincident(g11,g8)
    c: Horizontal(g8)
    c: Horizontal(g10)
    c: Vertical(g9)
    c: Vertical(g11)
    c: Coincident(g12,g13)
    c: Coincident(g13,g14)
    c: Coincident(g14,g15)
    c: Coincident(g15,g12)
    c: Horizontal(g12)
    c: Horizontal(g14)
    c: Vertical(g13)
    c: Vertical(g15)
    c: Coincident(g16,g17)
    c: Coincident(g17,g18)
    c: Coincident(g18,g19)
    c: Coincident(g19,g16)
    c: Horizontal(g16)
    c: Horizontal(g18)
    c: Vertical(g17)
    c: Vertical(g19)
    c: Coincident(g20,g21)
    c: Coincident(g21,g22)
    c: Coincident(g22,g23)
    c: Coincident(g23,g20)
    c: Horizontal(g20)
    c: Horizontal(g22)
    c: Vertical(g21)
    c: Vertical(g23)
    c: DistanceY(g8,g12) = 50
    c: DistanceX(g8,g12) = 50
    c: DistanceX(g21,g17) = 50
    c: DistanceY(g21,g17) = 50
    c: DistanceY(g16,g20) = 50
    c: DistanceY(g10,g14) = -50
    c: Equal(g23,g15)
    c: DistanceX(g12,g20) = 0
    c: DistanceX(g13,g20) = 0
    c: DistanceX(g4,g8) = 2.5
    c: DistanceY(g4,g8) = 2.5
    c: DistanceX(g6,g18) = -2.5
    c: DistanceY(g6,g18) = -2.5
    c: DistanceY(g10,g16) = 2.5
    c: PointOnObject(g9,g17)
    c: PointOnObject(g16,g11)
FEATURE [Part::FeaturePython] Window006  # Arch/BIM 170 (typed FeaturePython)
  Area = 1161288
  Base = -> Sketch009
  Frame = 50.8
  GlobalId = 1oje5truX3HfOa1dXVWm9J
  Height = 1524
  HoleDepth = 0
  HoleWire = 0
  HorizontalArea = 0
  Hosts = -> [Wall]
  IfcData = IfcUID=1oje5truX3HfOa1dXVWm9J,+2 more (map truncated)
  IfcType = 170
  LouvreSpacing = 0
  LouvreWidth = 0
  MoveBase = false
  MoveWithHost = true
  Normal = (1,0,0)
  Opening = 0
  OverallHeight = 1524
  OverallWidth = 762
  PartitioningType = 0
  PerimeterLength = 0
  PredefinedType = 0
  Preset = 4
  SymbolElevation = false
  SymbolPlan = false
  VerticalArea = 0
  Width = 762
  WindowParts = <same value as first occurrence — deduplicated (x10 in doc)>
  expr: OverallHeight = .Height.Value
  expr: OverallWidth = .Width.Value
FEATURE [Sketcher::SketchObject] Sketch010
  ArcFitTolerance = 1e-06
  ExternalTypes = [0]
  FullyConstrained = true
  MakeInternals = false
  Placement = pos=(1970.5,13565,609.6) rot=(0.57735,-0.57735,-0.57735;2.0944rad)
  sketch-geometry (24):
    g0: LineSegment StartX=0 StartY=0 StartZ=0 EndX=762 EndY=0 EndZ=0
    g1: LineSegment StartX=762 StartY=0 StartZ=0 EndX=762 EndY=1524 EndZ=0
    g2: LineSegment StartX=762 StartY=1524 StartZ=0 EndX=0 EndY=1524 EndZ=0
    g3: LineSegment StartX=0 StartY=1524 StartZ=0 EndX=0 EndY=0 EndZ=0
    g4: LineSegment StartX=25 StartY=25 StartZ=0 EndX=737 EndY=25 EndZ=0
    g5: LineSegment StartX=737 StartY=25 StartZ=0 EndX=737 EndY=1499 EndZ=0
    g6: LineSegment StartX=737 StartY=1499 StartZ=0 EndX=25 EndY=1499 EndZ=0
    g7: LineSegment StartX=25 StartY=1499 StartZ=0 EndX=25 EndY=25 EndZ=0
    g8: LineSegment StartX=27.5 StartY=27.5 StartZ=0 EndX=734.5 EndY=27.5 EndZ=0
    g9: LineSegment StartX=734.5 StartY=27.5 StartZ=0 EndX=734.5 EndY=760.75 EndZ=0
    g10: LineSegment StartX=734.5 StartY=760.75 StartZ=0 EndX=27.5 EndY=760.75 EndZ=0
    g11: LineSegment StartX=27.5 StartY=760.75 StartZ=0 EndX=27.5 EndY=27.5 EndZ=0
    g12: LineSegment StartX=77.5 StartY=77.5 StartZ=0 EndX=684.5 EndY=77.5 EndZ=0
    g13: LineSegment StartX=684.5 StartY=77.5 StartZ=0 EndX=684.5 EndY=710.75 EndZ=0
    g14: LineSegment StartX=684.5 StartY=710.75 StartZ=0 EndX=77.5 EndY=710.75 EndZ=0
    g15: LineSegment StartX=77.5 StartY=710.75 StartZ=0 EndX=77.5 EndY=77.5 EndZ=0
    g16: LineSegment StartX=27.5 StartY=763.25 StartZ=0 EndX=734.5 EndY=763.25 EndZ=0
    g17: LineSegment StartX=734.5 StartY=763.25 StartZ=0 EndX=734.5 EndY=1496.5 EndZ=0
    g18: LineSegment StartX=734.5 StartY=1496.5 StartZ=0 EndX=27.5 EndY=1496.5 EndZ=0
    g19: LineSegment StartX=27.5 StartY=1496.5 StartZ=0 EndX=27.5 EndY=763.25 EndZ=0
    g20: LineSegment StartX=77.5 StartY=813.25 StartZ=0 EndX=684.5 EndY=813.25 EndZ=0
    g21: LineSegment StartX=684.5 StartY=813.25 StartZ=0 EndX=684.5 EndY=1446.5 EndZ=0
    g22: LineSegment StartX=684.5 StartY=1446.5 StartZ=0 EndX=77.5 EndY=1446.5 EndZ=0
    g23: LineSegment StartX=77.5 StartY=1446.5 StartZ=0 EndX=77.5 EndY=813.25 EndZ=0
  constraints (71):
    c: Coincident(g0,g1)
    c: Coincident(g1,g2)
    c: Coincident(g2,g3)
    c: Coincident(g3,g0)
    c: Horizontal(g0)
    c: Horizontal(g2)
    c: Vertical(g1)
    c: Vertical(g3)
    c: Coincident(g4,g5)
    c: Coincident(g5,g6)
    c: Coincident(g6,g7)
    c: Coincident(g7,g4)
    c: Horizontal(g4)
    c: Horizontal(g6)
    c: Vertical(g5)
    c: Vertical(g7)
    c: DistanceY(g1) = 1524  'Height'
    c: DistanceX(g0) = 762  'Width'
    c: DistanceY(g6,g2) = 25  'Frame1'
    c: DistanceX(g2,g6) = 25  'Frame2'
    c: DistanceX(g4,g0) = 25  'Frame3'
    c: DistanceY(g0,g4) = 25  'Frame4'
    c: Coincident(g0,g-1)
    c: Coincident(g8,g9)
    c: Coincident(g9,g10)
    c: Coincident(g10,g11)
    c: Coincident(g11,g8)
    c: Horizontal(g8)
    c: Horizontal(g10)
    c: Vertical(g9)
    c: Vertical(g11)
    c: Coincident(g12,g13)
    c: Coincident(g13,g14)
    c: Coincident(g14,g15)
    c: Coincident(g15,g12)
    c: Horizontal(g12)
    c: Horizontal(g14)
    c: Vertical(g13)
    c: Vertical(g15)
    c: Coincident(g16,g17)
    c: Coincident(g17,g18)
    c: Coincident(g18,g19)
    c: Coincident(g19,g16)
    c: Horizontal(g16)
    c: Horizontal(g18)
    c: Vertical(g17)
    c: Vertical(g19)
    c: Coincident(g20,g21)
    c: Coincident(g21,g22)
    c: Coincident(g22,g23)
    c: Coincident(g23,g20)
    c: Horizontal(g20)
    c: Horizontal(g22)
    c: Vertical(g21)
    c: Vertical(g23)
    c: DistanceY(g8,g12) = 50
    c: DistanceX(g8,g12) = 50
    c: DistanceX(g21,g17) = 50
    c: DistanceY(g21,g17) = 50
    c: DistanceY(g16,g20) = 50
    c: DistanceY(g10,g14) = -50
    c: Equal(g23,g15)
    c: DistanceX(g12,g20) = 0
    c: DistanceX(g13,g20) = 0
    c: DistanceX(g4,g8) = 2.5
    c: DistanceY(g4,g8) = 2.5
    c: DistanceX(g6,g18) = -2.5
    c: DistanceY(g6,g18) = -2.5
    c: DistanceY(g10,g16) = 2.5
    c: PointOnObject(g9,g17)
    c: PointOnObject(g16,g11)
FEATURE [Part::FeaturePython] Window007  # Arch/BIM 170 (typed FeaturePython)
  Area = 1161288
  Base = -> Sketch010
  Frame = 50.8
  GlobalId = 3$7C_7mwjEJuQ8ShL_W5eh
  Height = 1524
  HoleDepth = 0
  HoleWire = 0
  HorizontalArea = 0
  Hosts = -> [Wall]
  IfcData = IfcUID=3$7C_7mwjEJuQ8ShL_W5eh,+2 more (map truncated)
  IfcType = 170
  LouvreSpacing = 0
  LouvreWidth = 0
  MoveBase = false
  MoveWithHost = true
  Normal = (1,0,0)
  Opening = 0
  OverallHeight = 1524
  OverallWidth = 762
  PartitioningType = 0
  PerimeterLength = 0
  PredefinedType = 0
  Preset = 4
  SymbolElevation = false
  SymbolPlan = false
  VerticalArea = 0
  Width = 762
  WindowParts = <same value as first occurrence — deduplicated (x10 in doc)>
  expr: OverallHeight = .Height.Value
  expr: OverallWidth = .Width.Value
FEATURE [Sketcher::SketchObject] Sketch011
  ArcFitTolerance = 1e-06
  ExternalTypes = [0]
  FullyConstrained = true
  MakeInternals = false
  Placement = pos=(5181.22,11745.8,609.6) rot=(1,0,0;1.5708rad)
  sketch-geometry (24):
    g0: LineSegment StartX=0 StartY=0 StartZ=0 EndX=762 EndY=0 EndZ=0
    g1: LineSegment StartX=762 StartY=0 StartZ=0 EndX=762 EndY=1524 EndZ=0
    g2: LineSegment StartX=762 StartY=1524 StartZ=0 EndX=0 EndY=1524 EndZ=0
    g3: LineSegment StartX=0 StartY=1524 StartZ=0 EndX=0 EndY=0 EndZ=0
    g4: LineSegment StartX=25 StartY=25 StartZ=0 EndX=737 EndY=25 EndZ=0
    g5: LineSegment StartX=737 StartY=25 StartZ=0 EndX=737 EndY=1499 EndZ=0
    g6: LineSegment StartX=737 StartY=1499 StartZ=0 EndX=25 EndY=1499 EndZ=0
    g7: LineSegment StartX=25 StartY=1499 StartZ=0 EndX=25 EndY=25 EndZ=0
    g8: LineSegment StartX=27.5 StartY=27.5 StartZ=0 EndX=734.5 EndY=27.5 EndZ=0
    g9: LineSegment StartX=734.5 StartY=27.5 StartZ=0 EndX=734.5 EndY=760.75 EndZ=0
    g10: LineSegment StartX=734.5 StartY=760.75 StartZ=0 EndX=27.5 EndY=760.75 EndZ=0
    g11: LineSegment StartX=27.5 StartY=760.75 StartZ=0 EndX=27.5 EndY=27.5 EndZ=0
    g12: LineSegment StartX=77.5 StartY=77.5 StartZ=0 EndX=684.5 EndY=77.5 EndZ=0
    g13: LineSegment StartX=684.5 StartY=77.5 StartZ=0 EndX=684.5 EndY=710.75 EndZ=0
    g14: LineSegment StartX=684.5 StartY=710.75 StartZ=0 EndX=77.5 EndY=710.75 EndZ=0
    g15: LineSegment StartX=77.5 StartY=710.75 StartZ=0 EndX=77.5 EndY=77.5 EndZ=0
    g16: LineSegment StartX=27.5 StartY=763.25 StartZ=0 EndX=734.5 EndY=763.25 EndZ=0
    g17: LineSegment StartX=734.5 StartY=763.25 StartZ=0 EndX=734.5 EndY=1496.5 EndZ=0
    g18: LineSegment StartX=734.5 StartY=1496.5 StartZ=0 EndX=27.5 EndY=1496.5 EndZ=0
    g19: LineSegment StartX=27.5 StartY=1496.5 StartZ=0 EndX=27.5 EndY=763.25 EndZ=0
    g20: LineSegment StartX=77.5 StartY=813.25 StartZ=0 EndX=684.5 EndY=813.25 EndZ=0
    g21: LineSegment StartX=684.5 StartY=813.25 StartZ=0 EndX=684.5 EndY=1446.5 EndZ=0
    g22: LineSegment StartX=684.5 StartY=1446.5 StartZ=0 EndX=77.5 EndY=1446.5 EndZ=0
    g23: LineSegment StartX=77.5 StartY=1446.5 StartZ=0 EndX=77.5 EndY=813.25 EndZ=0
  constraints (71):
    c: Coincident(g0,g1)
    c: Coincident(g1,g2)
    c: Coincident(g2,g3)
    c: Coincident(g3,g0)
    c: Horizontal(g0)
    c: Horizontal(g2)
    c: Vertical(g1)
    c: Vertical(g3)
    c: Coincident(g4,g5)
    c: Coincident(g5,g6)
    c: Coincident(g6,g7)
    c: Coincident(g7,g4)
    c: Horizontal(g4)
    c: Horizontal(g6)
    c: Vertical(g5)
    c: Vertical(g7)
    c: DistanceY(g1) = 1524  'Height'
    c: DistanceX(g0) = 762  'Width'
    c: DistanceY(g6,g2) = 25  'Frame1'
    c: DistanceX(g2,g6) = 25  'Frame2'
    c: DistanceX(g4,g0) = 25  'Frame3'
    c: DistanceY(g0,g4) = 25  'Frame4'
    c: Coincident(g0,g-1)
    c: Coincident(g8,g9)
    c: Coincident(g9,g10)
    c: Coincident(g10,g11)
    c: Coincident(g11,g8)
    c: Horizontal(g8)
    c: Horizontal(g10)
    c: Vertical(g9)
    c: Vertical(g11)
    c: Coincident(g12,g13)
    c: Coincident(g13,g14)
    c: Coincident(g14,g15)
    c: Coincident(g15,g12)
    c: Horizontal(g12)
    c: Horizontal(g14)
    c: Vertical(g13)
    c: Vertical(g15)
    c: Coincident(g16,g17)
    c: Coincident(g17,g18)
    c: Coincident(g18,g19)
    c: Coincident(g19,g16)
    c: Horizontal(g16)
    c: Horizontal(g18)
    c: Vertical(g17)
    c: Vertical(g19)
    c: Coincident(g20,g21)
    c: Coincident(g21,g22)
    c: Coincident(g22,g23)
    c: Coincident(g23,g20)
    c: Horizontal(g20)
    c: Horizontal(g22)
    c: Vertical(g21)
    c: Vertical(g23)
    c: DistanceY(g8,g12) = 50
    c: DistanceX(g8,g12) = 50
    c: DistanceX(g21,g17) = 50
    c: DistanceY(g21,g17) = 50
    c: DistanceY(g16,g20) = 50
    c: DistanceY(g10,g14) = -50
    c: Equal(g23,g15)
    c: DistanceX(g12,g20) = 0
    c: DistanceX(g13,g20) = 0
    c: DistanceX(g4,g8) = 2.5
    c: DistanceY(g4,g8) = 2.5
    c: DistanceX(g6,g18) = -2.5
    c: DistanceY(g6,g18) = -2.5
    c: DistanceY(g10,g16) = 2.5
    c: PointOnObject(g9,g17)
    c: PointOnObject(g16,g11)
FEATURE [Sketcher::SketchObject] Sketch012
  ArcFitTolerance = 1e-06
  ExternalTypes = [0]
  FullyConstrained = true
  MakeInternals = false
  Placement = pos=(16690.4,11745.8,609.6) rot=(1,0,0;1.5708rad)
  sketch-geometry (24):
    g0: LineSegment StartX=0 StartY=0 StartZ=0 EndX=762 EndY=0 EndZ=0
    g1: LineSegment StartX=762 StartY=0 StartZ=0 EndX=762 EndY=1524 EndZ=0
    g2: LineSegment StartX=762 StartY=1524 StartZ=0 EndX=0 EndY=1524 EndZ=0
    g3: LineSegment StartX=0 StartY=1524 StartZ=0 EndX=0 EndY=0 EndZ=0
    g4: LineSegment StartX=25 StartY=25 StartZ=0 EndX=737 EndY=25 EndZ=0
    g5: LineSegment StartX=737 StartY=25 StartZ=0 EndX=737 EndY=1499 EndZ=0
    g6: LineSegment StartX=737 StartY=1499 StartZ=0 EndX=25 EndY=1499 EndZ=0
    g7: LineSegment StartX=25 StartY=1499 StartZ=0 EndX=25 EndY=25 EndZ=0
    g8: LineSegment StartX=27.5 StartY=27.5 StartZ=0 EndX=734.5 EndY=27.5 EndZ=0
    g9: LineSegment StartX=734.5 StartY=27.5 StartZ=0 EndX=734.5 EndY=760.75 EndZ=0
    g10: LineSegment StartX=734.5 StartY=760.75 StartZ=0 EndX=27.5 EndY=760.75 EndZ=0
    g11: LineSegment StartX=27.5 StartY=760.75 StartZ=0 EndX=27.5 EndY=27.5 EndZ=0
    g12: LineSegment StartX=77.5 StartY=77.5 StartZ=0 EndX=684.5 EndY=77.5 EndZ=0
    g13: LineSegment StartX=684.5 StartY=77.5 StartZ=0 EndX=684.5 EndY=710.75 EndZ=0
    g14: LineSegment StartX=684.5 StartY=710.75 StartZ=0 EndX=77.5 EndY=710.75 EndZ=0
    g15: LineSegment StartX=77.5 StartY=710.75 StartZ=0 EndX=77.5 EndY=77.5 EndZ=0
    g16: LineSegment StartX=27.5 StartY=763.25 StartZ=0 EndX=734.5 EndY=763.25 EndZ=0
    g17: LineSegment StartX=734.5 StartY=763.25 StartZ=0 EndX=734.5 EndY=1496.5 EndZ=0
    g18: LineSegment StartX=734.5 StartY=1496.5 StartZ=0 EndX=27.5 EndY=1496.5 EndZ=0
    g19: LineSegment StartX=27.5 StartY=1496.5 StartZ=0 EndX=27.5 EndY=763.25 EndZ=0
    g20: LineSegment StartX=77.5 StartY=813.25 StartZ=0 EndX=684.5 EndY=813.25 EndZ=0
    g21: LineSegment StartX=684.5 StartY=813.25 StartZ=0 EndX=684.5 EndY=1446.5 EndZ=0
    g22: LineSegment StartX=684.5 StartY=1446.5 StartZ=0 EndX=77.5 EndY=1446.5 EndZ=0
    g23: LineSegment StartX=77.5 StartY=1446.5 StartZ=0 EndX=77.5 EndY=813.25 EndZ=0
  constraints (71):
    c: Coincident(g0,g1)
    c: Coincident(g1,g2)
    c: Coincident(g2,g3)
    c: Coincident(g3,g0)
    c: Horizontal(g0)
    c: Horizontal(g2)
    c: Vertical(g1)
    c: Vertical(g3)
    c: Coincident(g4,g5)
    c: Coincident(g5,g6)
    c: Coincident(g6,g7)
    c: Coincident(g7,g4)
    c: Horizontal(g4)
    c: Horizontal(g6)
    c: Vertical(g5)
    c: Vertical(g7)
    c: DistanceY(g1) = 1524  'Height'
    c: DistanceX(g0) = 762  'Width'
    c: DistanceY(g6,g2) = 25  'Frame1'
    c: DistanceX(g2,g6) = 25  'Frame2'
    c: DistanceX(g4,g0) = 25  'Frame3'
    c: DistanceY(g0,g4) = 25  'Frame4'
    c: Coincident(g0,g-1)
    c: Coincident(g8,g9)
    c: Coincident(g9,g10)
    c: Coincident(g10,g11)
    c: Coincident(g11,g8)
    c: Horizontal(g8)
    c: Horizontal(g10)
    c: Vertical(g9)
    c: Vertical(g11)
    c: Coincident(g12,g13)
    c: Coincident(g13,g14)
    c: Coincident(g14,g15)
    c: Coincident(g15,g12)
    c: Horizontal(g12)
    c: Horizontal(g14)
    c: Vertical(g13)
    c: Vertical(g15)
    c: Coincident(g16,g17)
    c: Coincident(g17,g18)
    c: Coincident(g18,g19)
    c: Coincident(g19,g16)
    c: Horizontal(g16)
    c: Horizontal(g18)
    c: Vertical(g17)
    c: Vertical(g19)
    c: Coincident(g20,g21)
    c: Coincident(g21,g22)
    c: Coincident(g22,g23)
    c: Coincident(g23,g20)
    c: Horizontal(g20)
    c: Horizontal(g22)
    c: Vertical(g21)
    c: Vertical(g23)
    c: DistanceY(g8,g12) = 50
    c: DistanceX(g8,g12) = 50
    c: DistanceX(g21,g17) = 50
    c: DistanceY(g21,g17) = 50
    c: DistanceY(g16,g20) = 50
    c: DistanceY(g10,g14) = -50
    c: Equal(g23,g15)
    c: DistanceX(g12,g20) = 0
    c: DistanceX(g13,g20) = 0
    c: DistanceX(g4,g8) = 2.5
    c: DistanceY(g4,g8) = 2.5
    c: DistanceX(g6,g18) = -2.5
    c: DistanceY(g6,g18) = -2.5
    c: DistanceY(g10,g16) = 2.5
    c: PointOnObject(g9,g17)
    c: PointOnObject(g16,g11)
FEATURE [Part::FeaturePython] Window009  # Arch/BIM 170 (typed FeaturePython)
  Area = 1161288
  Base = -> Sketch012
  Frame = 50.8
  GlobalId = 2jpbH3nmT4zv4$aONWCXgt
  Height = 1524
  HoleDepth = 0
  HoleWire = 0
  HorizontalArea = 0
  Hosts = -> [Wall]
  IfcData = IfcUID=2jpbH3nmT4zv4$aONWCXgt,+2 more (map truncated)
  IfcType = 170
  LouvreSpacing = 0
  LouvreWidth = 0
  MoveBase = false
  MoveWithHost = true
  Normal = (0,1,-2e-16)
  Opening = 0
  OverallHeight = 1524
  OverallWidth = 762
  PartitioningType = 0
  PerimeterLength = 0
  PredefinedType = 0
  Preset = 4
  SymbolElevation = false
  SymbolPlan = false
  VerticalArea = 0
  Width = 762
  WindowParts = <same value as first occurrence — deduplicated (x10 in doc)>
  expr: OverallHeight = .Height.Value
  expr: OverallWidth = .Width.Value
FEATURE [Sketcher::SketchObject] Sketch014
  ArcFitTolerance = 1e-06
  ExternalTypes = [0]
  FullyConstrained = true
  MakeInternals = false
  Placement = pos=(17039.4,15367.5,0) rot=(1,0,0;1.5708rad)
  sketch-geometry (8):
    g0: LineSegment StartX=0 StartY=0 StartZ=0 EndX=914.4 EndY=0 EndZ=0
    g1: LineSegment StartX=914.4 StartY=0 StartZ=0 EndX=914.4 EndY=2032 EndZ=0
    g2: LineSegment StartX=914.4 StartY=2032 StartZ=0 EndX=0 EndY=2032 EndZ=0
    g3: LineSegment StartX=0 StartY=2032 StartZ=0 EndX=0 EndY=0 EndZ=0
    g4: LineSegment StartX=25 StartY=0 StartZ=0 EndX=889.4 EndY=0 EndZ=0
    g5: LineSegment StartX=889.4 StartY=0 StartZ=0 EndX=889.4 EndY=2007 EndZ=0
    g6: LineSegment StartX=889.4 StartY=2007 StartZ=0 EndX=25 EndY=2007 EndZ=0
    g7: LineSegment StartX=25 StartY=2007 StartZ=0 EndX=25 EndY=0 EndZ=0
  constraints (23):
    c: Coincident(g0,g1)
    c: Coincident(g1,g2)
    c: Coincident(g2,g3)
    c: Coincident(g3,g0)
    c: Horizontal(g0)
    c: Horizontal(g2)
    c: Vertical(g1)
    c: Vertical(g3)
    c: Coincident(g4,g5)
    c: Coincident(g5,g6)
    c: Coincident(g6,g7)
    c: Coincident(g7,g4)
    c: Horizontal(g4)
    c: Horizontal(g6)
    c: Vertical(g5)
    c: Vertical(g7)
    c: DistanceY(g1) = 2032  'Height'
    c: DistanceX(g0) = 914.4  'Width'
    c: DistanceY(g6,g2) = 25  'Frame1'
    c: DistanceX(g2,g6) = 25  'Frame2'
    c: DistanceX(g4,g0) = 25  'Frame3'
    c: DistanceY(g0,g4) = 0
    c: Coincident(g0,g-1)
FEATURE [Part::FeaturePython] Window010  label="Door"  # Arch/BIM 41 (typed FeaturePython)
  Area = 1.85806e+06
  Base = -> Sketch014
  Frame = 50.8
  GlobalId = 0S$Fny44j32A1z9ZeJL$fS
  Height = 2032
  HoleDepth = 0
  HoleWire = 0
  HorizontalArea = 0
  Hosts = -> [Wall001]
  IfcData = IfcUID=0S$Fny44j32A1z9ZeJL$fS,+2 more (map truncated)
  IfcType = 41
  LouvreSpacing = 0
  LouvreWidth = 0
  MoveBase = false
  MoveWithHost = true
  Normal = (0,1,-2e-16)
  Opening = 0
  OperationType = 0
  OverallHeight = 2032
  OverallWidth = 914.4
  PerimeterLength = 0
  PredefinedType = 0
  Preset = 6
  SymbolElevation = false
  SymbolPlan = false
  VerticalArea = 0
  Width = 914.4
  WindowParts = OuterFrame | Frame | Wire0,Wire1 | -90.8+V | 0.00+V | Door | Solid panel | Wire1,Edge8,Mode1 | 50.8 | 25.0+V
  expr: OverallHeight = .Height.Value
  expr: OverallWidth = .Width.Value
FEATURE [Sketcher::SketchObject] Sketch015
  ArcFitTolerance = 1e-06
  ExternalTypes = [0]
  FullyConstrained = true
  MakeInternals = false
  Placement = pos=(12149.3,15367.5,0) rot=(1,0,0;1.5708rad)
  sketch-geometry (8):
    g0: LineSegment StartX=0 StartY=0 StartZ=0 EndX=914.4 EndY=0 EndZ=0
    g1: LineSegment StartX=914.4 StartY=0 StartZ=0 EndX=914.4 EndY=2032 EndZ=0
    g2: LineSegment StartX=914.4 StartY=2032 StartZ=0 EndX=0 EndY=2032 EndZ=0
    g3: LineSegment StartX=0 StartY=2032 StartZ=0 EndX=0 EndY=0 EndZ=0
    g4: LineSegment StartX=25 StartY=0 StartZ=0 EndX=889.4 EndY=0 EndZ=0
    g5: LineSegment StartX=889.4 StartY=0 StartZ=0 EndX=889.4 EndY=2007 EndZ=0
    g6: LineSegment StartX=889.4 StartY=2007 StartZ=0 EndX=25 EndY=2007 EndZ=0
    g7: LineSegment StartX=25 StartY=2007 StartZ=0 EndX=25 EndY=0 EndZ=0
  constraints (23):
    c: Coincident(g0,g1)
    c: Coincident(g1,g2)
    c: Coincident(g2,g3)
    c: Coincident(g3,g0)
    c: Horizontal(g0)
    c: Horizontal(g2)
    c: Vertical(g1)
    c: Vertical(g3)
    c: Coincident(g4,g5)
    c: Coincident(g5,g6)
    c: Coincident(g6,g7)
    c: Coincident(g7,g4)
    c: Horizontal(g4)
    c: Horizontal(g6)
    c: Vertical(g5)
    c: Vertical(g7)
    c: DistanceY(g1) = 2032  'Height'
    c: DistanceX(g0) = 914.4  'Width'
    c: DistanceY(g6,g2) = 25  'Frame1'
    c: DistanceX(g2,g6) = 25  'Frame2'
    c: DistanceX(g4,g0) = 25  'Frame3'
    c: DistanceY(g0,g4) = 0
    c: Coincident(g0,g-1)
FEATURE [Part::FeaturePython] Window011  label="Door001"  # Arch/BIM 41 (typed FeaturePython)
  Area = 1.85806e+06
  Base = -> Sketch015
  Frame = 50.8
  GlobalId = 3X$wLCsRz8NvdbizO$lpoD
  Height = 2032
  HoleDepth = 0
  HoleWire = 0
  HorizontalArea = 0
  Hosts = -> [Wall001]
  IfcData = IfcUID=3X$wLCsRz8NvdbizO$lpoD,+2 more (map truncated)
  IfcType = 41
  LouvreSpacing = 0
  LouvreWidth = 0
  MoveBase = false
  MoveWithHost = true
  Normal = (0,1,-2e-16)
  Opening = 0
  OperationType = 0
  OverallHeight = 2032
  OverallWidth = 914.4
  PerimeterLength = 0
  PredefinedType = 0
  Preset = 6
  SymbolElevation = false
  SymbolPlan = false
  VerticalArea = 0
  Width = 914.4
  WindowParts = OuterFrame | Frame | Wire0,Wire1 | -90.8+V | 0.00+V | Door | Solid panel | Wire1,Edge8,Mode1 | 50.8 | 25.0+V
  expr: OverallHeight = .Height.Value
  expr: OverallWidth = .Width.Value
FEATURE [Sketcher::SketchObject] Sketch016
  ArcFitTolerance = 1e-06
  ExternalTypes = [0]
  FullyConstrained = true
  MakeInternals = false
  Placement = pos=(8257.75,13144.6,0) rot=(0.57735,0.57735,0.57735;2.0944rad)
  sketch-geometry (8):
    g0: LineSegment StartX=0 StartY=0 StartZ=0 EndX=914.4 EndY=0 EndZ=0
    g1: LineSegment StartX=914.4 StartY=0 StartZ=0 EndX=914.4 EndY=2032 EndZ=0
    g2: LineSegment StartX=914.4 StartY=2032 StartZ=0 EndX=0 EndY=2032 EndZ=0
    g3: LineSegment StartX=0 StartY=2032 StartZ=0 EndX=0 EndY=0 EndZ=0
    g4: LineSegment StartX=25 StartY=0 StartZ=0 EndX=889.4 EndY=0 EndZ=0
    g5: LineSegment StartX=889.4 StartY=0 StartZ=0 EndX=889.4 EndY=2007 EndZ=0
    g6: LineSegment StartX=889.4 StartY=2007 StartZ=0 EndX=25 EndY=2007 EndZ=0
    g7: LineSegment StartX=25 StartY=2007 StartZ=0 EndX=25 EndY=0 EndZ=0
  constraints (23):
    c: Coincident(g0,g1)
    c: Coincident(g1,g2)
    c: Coincident(g2,g3)
    c: Coincident(g3,g0)
    c: Horizontal(g0)
    c: Horizontal(g2)
    c: Vertical(g1)
    c: Vertical(g3)
    c: Coincident(g4,g5)
    c: Coincident(g5,g6)
    c: Coincident(g6,g7)
    c: Coincident(g7,g4)
    c: Horizontal(g4)
    c: Horizontal(g6)
    c: Vertical(g5)
    c: Vertical(g7)
    c: DistanceY(g1) = 2032  'Height'
    c: DistanceX(g0) = 914.4  'Width'
    c: DistanceY(g6,g2) = 25  'Frame1'
    c: DistanceX(g2,g6) = 25  'Frame2'
    c: DistanceX(g4,g0) = 25  'Frame3'
    c: DistanceY(g0,g4) = 0
    c: Coincident(g0,g-1)
FEATURE [Part::FeaturePython] Window012  label="Door002"  # Arch/BIM 41 (typed FeaturePython)
  Area = 1.85806e+06
  Base = -> Sketch016
  Frame = 50.8
  GlobalId = 2aFbaveRP9Nw8U53cdFzTQ
  Height = 2032
  HoleDepth = 0
  HoleWire = 0
  HorizontalArea = 0
  Hosts = -> [Wall001]
  IfcData = IfcUID=2aFbaveRP9Nw8U53cdFzTQ,+2 more (map truncated)
  IfcType = 41
  LouvreSpacing = 0
  LouvreWidth = 0
  MoveBase = false
  MoveWithHost = true
  Normal = (-1,0,0)
  Opening = 0
  OperationType = 0
  OverallHeight = 2032
  OverallWidth = 914.4
  PerimeterLength = 0
  PredefinedType = 0
  Preset = 6
  SymbolElevation = false
  SymbolPlan = false
  VerticalArea = 0
  Width = 914.4
  WindowParts = OuterFrame | Frame | Wire0,Wire1 | -90.8+V | 0.00+V | Door | Solid panel | Wire1,Edge8,Mode1 | 50.8 | 25.0+V
  expr: OverallHeight = .Height.Value
  expr: OverallWidth = .Width.Value
FEATURE [Spreadsheet::Sheet] IfcProperties
  cells = A1='Category; B1='Key; C1='Type; D1='Value; E1='Unit
FEATURE [App::DocumentObjectGroup] IfcPropertiesContainer
  Group = -> [IfcProperties]
FEATURE [Sketcher::SketchObject] Sketch017
  ArcFitTolerance = 1e-06
  ExternalGeometry = -> [Sketch001]
  ExternalTypes = [0]
  FullyConstrained = false
  MakeInternals = false
  sketch-geometry (1):
    g0: LineSegment StartX=23456.9 StartY=20576.5 StartZ=0 EndX=31640.2 EndY=20576.5 EndZ=0
  constraints (2):
    c: Coincident(g0,g-3)
    c: Horizontal(g0)
FEATURE [Part::FeaturePython] Wall002  # Arch/BIM 166 (typed FeaturePython)
  Align = 0
  ArchSketchData = true
  ArchSketchPropertySet = 0
  Area = 2.455e+07
  Base = -> Sketch017
  BlockHeight = 0
  BlockLength = 0
  CountBroken = 0
  CountEntire = 0
  Face = 0
  GlobalId = 2supB_x_P7p9Qbklddn78J
  Height = 3000
  HorizontalArea = 1.24714e+06
  IfcData = IfcUID=2supB_x_P7p9Qbklddn78J,+2 more (map truncated)
  IfcType = 166
  Joint = 0
  Length = 8183.33
  MakeBlocks = false
  MoveBase = false
  MoveWithHost = false
  Normal = (0,0,0)
  OffsetFirst = 0
  OffsetSecond = 0
  PerimeterLength = 16671.5
  PredefinedType = 0
  VerticalArea = 5.00144e+07
  Width = 152.4
FEATURE [App::DocumentObjectGroup] Group  label="Walls"
  Group = -> [Wall001,Wall,Wall002]
FEATURE [Sketcher::SketchObject] Sketch019
  ArcFitTolerance = 1e-06
  ExternalTypes = [0]
  FullyConstrained = true
  MakeInternals = false
  Placement = pos=(2989.2,20576.5,609.6) rot=(0,0.707107,0.707107;3.14159rad)
  sketch-geometry (24):
    g0: LineSegment StartX=0 StartY=0 StartZ=0 EndX=765 EndY=0 EndZ=0
    g1: LineSegment StartX=765 StartY=0 StartZ=0 EndX=765 EndY=1962 EndZ=0
    g2: LineSegment StartX=765 StartY=1962 StartZ=0 EndX=0 EndY=1962 EndZ=0
    g3: LineSegment StartX=0 StartY=1962 StartZ=0 EndX=0 EndY=0 EndZ=0
    g4: LineSegment StartX=25 StartY=25 StartZ=0 EndX=740 EndY=25 EndZ=0
    g5: LineSegment StartX=740 StartY=25 StartZ=0 EndX=740 EndY=1937 EndZ=0
    g6: LineSegment StartX=740 StartY=1937 StartZ=0 EndX=25 EndY=1937 EndZ=0
    g7: LineSegment StartX=25 StartY=1937 StartZ=0 EndX=25 EndY=25 EndZ=0
    g8: LineSegment StartX=27.5 StartY=27.5 StartZ=0 EndX=737.5 EndY=27.5 EndZ=0
    g9: LineSegment StartX=737.5 StartY=27.5 StartZ=0 EndX=737.5 EndY=979.75 EndZ=0
    g10: LineSegment StartX=737.5 StartY=979.75 StartZ=0 EndX=27.5 EndY=979.75 EndZ=0
    g11: LineSegment StartX=27.5 StartY=979.75 StartZ=0 EndX=27.5 EndY=27.5 EndZ=0
    g12: LineSegment StartX=77.5 StartY=77.5 StartZ=0 EndX=687.5 EndY=77.5 EndZ=0
    g13: LineSegment StartX=687.5 StartY=77.5 StartZ=0 EndX=687.5 EndY=929.75 EndZ=0
    g14: LineSegment StartX=687.5 StartY=929.75 StartZ=0 EndX=77.5 EndY=929.75 EndZ=0
    g15: LineSegment StartX=77.5 StartY=929.75 StartZ=0 EndX=77.5 EndY=77.5 EndZ=0
    g16: LineSegment StartX=27.5 StartY=982.25 StartZ=0 EndX=737.5 EndY=982.25 EndZ=0
    g17: LineSegment StartX=737.5 StartY=982.25 StartZ=0 EndX=737.5 EndY=1934.5 EndZ=0
    g18: LineSegment StartX=737.5 StartY=1934.5 StartZ=0 EndX=27.5 EndY=1934.5 EndZ=0
    g19: LineSegment StartX=27.5 StartY=1934.5 StartZ=0 EndX=27.5 EndY=982.25 EndZ=0
    g20: LineSegment StartX=77.5 StartY=1032.25 StartZ=0 EndX=687.5 EndY=1032.25 EndZ=0
    g21: LineSegment StartX=687.5 StartY=1032.25 StartZ=0 EndX=687.5 EndY=1884.5 EndZ=0
    g22: LineSegment StartX=687.5 StartY=1884.5 StartZ=0 EndX=77.5 EndY=1884.5 EndZ=0
    g23: LineSegment StartX=77.5 StartY=1884.5 StartZ=0 EndX=77.5 EndY=1032.25 EndZ=0
  constraints (71):
    c: Coincident(g0,g1)
    c: Coincident(g1,g2)
    c: Coincident(g2,g3)
    c: Coincident(g3,g0)
    c: Horizontal(g0)
    c: Horizontal(g2)
    c: Vertical(g1)
    c: Vertical(g3)
    c: Coincident(g4,g5)
    c: Coincident(g5,g6)
    c: Coincident(g6,g7)
    c: Coincident(g7,g4)
    c: Horizontal(g4)
    c: Horizontal(g6)
    c: Vertical(g5)
    c: Vertical(g7)
    c: DistanceY(g1) = 1962  'Height'
    c: DistanceX(g0) = 765  'Width'
    c: DistanceY(g6,g2) = 25  'Frame1'
    c: DistanceX(g2,g6) = 25  'Frame2'
    c: DistanceX(g4,g0) = 25  'Frame3'
    c: DistanceY(g0,g4) = 25  'Frame4'
    c: Coincident(g0,g-1)
    c: Coincident(g8,g9)
    c: Coincident(g9,g10)
    c: Coincident(g10,g11)
    c: Coincident(g11,g8)
    c: Horizontal(g8)
    c: Horizontal(g10)
    c: Vertical(g9)
    c: Vertical(g11)
    c: Coincident(g12,g13)
    c: Coincident(g13,g14)
    c: Coincident(g14,g15)
    c: Coincident(g15,g12)
    c: Horizontal(g12)
    c: Horizontal(g14)
    c: Vertical(g13)
    c: Vertical(g15)
    c: Coincident(g16,g17)
    c: Coincident(g17,g18)
    c: Coincident(g18,g19)
    c: Coincident(g19,g16)
    c: Horizontal(g16)
    c: Horizontal(g18)
    c: Vertical(g17)
    c: Vertical(g19)
    c: Coincident(g20,g21)
    c: Coincident(g21,g22)
    c: Coincident(g22,g23)
    c: Coincident(g23,g20)
    c: Horizontal(g20)
    c: Horizontal(g22)
    c: Vertical(g21)
    c: Vertical(g23)
    c: DistanceY(g8,g12) = 50
    c: DistanceX(g8,g12) = 50
    c: DistanceX(g21,g17) = 50
    c: DistanceY(g21,g17) = 50
    c: DistanceY(g16,g20) = 50
    c: DistanceY(g10,g14) = -50
    c: Equal(g23,g15)
    c: DistanceX(g12,g20) = 0
    c: DistanceX(g13,g20) = 0
    c: DistanceX(g4,g8) = 2.5
    c: DistanceY(g4,g8) = 2.5
    c: DistanceX(g6,g18) = -2.5
    c: DistanceY(g6,g18) = -2.5
    c: DistanceY(g10,g16) = 2.5
    c: PointOnObject(g9,g17)
    c: PointOnObject(g16,g11)
FEATURE [Part::FeaturePython] Space006  # Arch/BIM 122 (typed FeaturePython)
  Area = 3.02244e+07
  AreaCalculationType = 0
  AutoPower = false
  Boundaries = -> [Wall001,Wall]
  CompositionType = 0
  Conditioning = 0
  ElevationWithFlooring = -5e-15
  EquipmentPower = 0
  FloorThickness = 0
  GlobalId = 1ybWwR2T1Af8yBimRj0Wwd
  HorizontalArea = 3.02244e+07
  IfcData = IfcUID=1ybWwR2T1Af8yBimRj0Wwd,+2 more (map truncated)
  IfcType = 122
  Internal = true
  LightingPower = 0
  LongName = Space006
  MoveBase = false
  MoveWithHost = false
  NumberOfPeople = 0
  PerimeterLength = 22109.6
  PredefinedType = 0
  SpaceType = 0
  VerticalArea = 6.63287e+07
  expr: ElevationWithFlooring = .Shape.BoundBox.ZMin
FEATURE [Part::FeaturePython] Space007  # Arch/BIM 122 (typed FeaturePython)
  Area = 2.39344e+07
  AreaCalculationType = 0
  AutoPower = false
  Boundaries = -> [Wall001,Wall]
  CompositionType = 0
  Conditioning = 0
  ElevationWithFlooring = -5e-15
  EquipmentPower = 0
  FloorThickness = 0
  GlobalId = 03aBiX5Qn6WA74X8Cd2qXD
  HorizontalArea = 2.39344e+07
  IfcData = IfcUID=03aBiX5Qn6WA74X8Cd2qXD,+2 more (map truncated)
  IfcType = 122
  Internal = true
  LightingPower = 0
  LongName = Space007
  MoveBase = false
  MoveWithHost = false
  NumberOfPeople = 0
  PerimeterLength = 19570.7
  PredefinedType = 0
  SpaceType = 0
  VerticalArea = 5.87121e+07
  expr: ElevationWithFlooring = .Shape.BoundBox.ZMin
FEATURE [Part::FeaturePython] Window004  # Arch/BIM 170 (typed FeaturePython)
  Area = 1161288
  Base = -> Sketch007
  Frame = 50.8
  GlobalId = 2aG$l4v6H1TRfaTylLaGk9
  Height = 1524
  HoleDepth = 0
  HoleWire = 0
  HorizontalArea = 0
  Hosts = -> [Wall]
  IfcData = IfcUID=2aG$l4v6H1TRfaTylLaGk9,+2 more (map truncated)
  IfcType = 170
  LouvreSpacing = 0
  LouvreWidth = 0
  MoveBase = false
  MoveWithHost = true
  Normal = (0,-1,2e-16)
  Opening = 0
  OverallHeight = 1524
  OverallWidth = 762
  PartitioningType = 0
  PerimeterLength = 0
  PredefinedType = 0
  Preset = 4
  SymbolElevation = false
  SymbolPlan = false
  VerticalArea = 0
  Width = 762
  WindowParts = <same value as first occurrence — deduplicated (x10 in doc)>
  expr: OverallHeight = .Height.Value
  expr: OverallWidth = .Width.Value
FEATURE [Part::FeaturePython] Space008  # Arch/BIM 122 (typed FeaturePython)
  Area = 5.14388e+07
  AreaCalculationType = 0
  AutoPower = false
  Boundaries = -> [Wall,Wall001]
  CompositionType = 0
  Conditioning = 0
  ElevationWithFlooring = -5e-15
  EquipmentPower = 0
  FloorThickness = 0
  GlobalId = 0nHxQAwazFjRmTa4h1zqQK
  HorizontalArea = 5.14388e+07
  IfcData = IfcUID=0nHxQAwazFjRmTa4h1zqQK,+2 more (map truncated)
  IfcType = 122
  Internal = true
  LightingPower = 0
  LongName = Space008
  MoveBase = false
  MoveWithHost = false
  NumberOfPeople = 0
  PerimeterLength = 29118.3
  PredefinedType = 0
  SpaceType = 37
  VerticalArea = 8.73548e+07
  expr: ElevationWithFlooring = .Shape.BoundBox.ZMin
FEATURE [Part::FeaturePython] Window005  # Arch/BIM 170 (typed FeaturePython)
  Area = 1161288
  Base = -> Sketch008
  Frame = 50.8
  GlobalId = 2HfNGo35z5VxTZx3lYdv0K
  Height = 1524
  HoleDepth = 0
  HoleWire = 0
  HorizontalArea = 0
  Hosts = -> [Wall]
  IfcData = IfcUID=2HfNGo35z5VxTZx3lYdv0K,+2 more (map truncated)
  IfcType = 170
  LouvreSpacing = 0
  LouvreWidth = 0
  MoveBase = false
  MoveWithHost = true
  Normal = (0,-1,2e-16)
  Opening = 0
  OverallHeight = 1524
  OverallWidth = 762
  PartitioningType = 0
  PerimeterLength = 0
  PredefinedType = 0
  Preset = 4
  SymbolElevation = false
  SymbolPlan = false
  VerticalArea = 0
  Width = 762
  WindowParts = <same value as first occurrence — deduplicated (x10 in doc)>
  expr: OverallHeight = .Height.Value
  expr: OverallWidth = .Width.Value
FEATURE [Part::FeaturePython] Space011  # Arch/BIM 122 (typed FeaturePython)
  Area = 6.70011e+07
  AreaCalculationType = 0
  AutoPower = false
  Boundaries = -> [Wall,Wall001]
  CompositionType = 0
  Conditioning = 0
  ElevationWithFlooring = -1e-14
  EquipmentPower = 0
  FloorThickness = 0
  GlobalId = 3reOMqw$r9g8ThINodEakB
  HorizontalArea = 6.70011e+07
  IfcData = IfcUID=3reOMqw$r9g8ThINodEakB,+2 more (map truncated)
  IfcType = 122
  Internal = true
  LightingPower = 0
  LongName = Space011
  MoveBase = false
  MoveWithHost = false
  NumberOfPeople = 0
  PerimeterLength = 45563.3
  PredefinedType = 0
  SpaceType = 0
  VerticalArea = 1.3669e+08
  expr: ElevationWithFlooring = .Shape.BoundBox.ZMin
FEATURE [Part::FeaturePython] Space012  # Arch/BIM 122 (typed FeaturePython)
  Area = 4.26027e+07
  AreaCalculationType = 0
  AutoPower = false
  Boundaries = -> [Space011,Wall001]
  CompositionType = 0
  Conditioning = 0
  ElevationWithFlooring = -1e-14
  EquipmentPower = 0
  FloorThickness = 0
  GlobalId = 3wnJAG0VP3zhcMuPOm9Gh7
  HorizontalArea = 4.26027e+07
  IfcData = IfcUID=3wnJAG0VP3zhcMuPOm9Gh7,+2 more (map truncated)
  IfcType = 122
  Internal = true
  LightingPower = 0
  LongName = Space012
  MoveBase = false
  MoveWithHost = false
  NumberOfPeople = 0
  PerimeterLength = 26775.4
  PredefinedType = 0
  SpaceType = 0
  VerticalArea = 8.03263e+07
  expr: ElevationWithFlooring = .Shape.BoundBox.ZMin
FEATURE [Part::FeaturePython] Space  # Arch/BIM 122 (typed FeaturePython)
  Area = 3.11462e+07
  AreaCalculationType = 0
  AutoPower = false
  Boundaries = -> [Wall,Space011]
  CompositionType = 0
  Conditioning = 0
  ElevationWithFlooring = -5e-15
  EquipmentPower = 0
  FloorThickness = 0
  GlobalId = 3WqCLszIX5$RgUbFK29bAd
  HorizontalArea = 3.11462e+07
  IfcData = IfcUID=3WqCLszIX5$RgUbFK29bAd,+2 more (map truncated)
  IfcType = 122
  Internal = true
  LightingPower = 0
  LongName = Space
  MoveBase = false
  MoveWithHost = false
  NumberOfPeople = 0
  PerimeterLength = 22406.5
  PredefinedType = 0
  SpaceType = 0
  VerticalArea = 6.72195e+07
  expr: ElevationWithFlooring = .Shape.BoundBox.ZMin
FEATURE [App::DocumentObjectGroup] Group002  label="Spaces"
  Group = -> [Space006,Space007,Space008,Space011,Space012,Space]
FEATURE [App::GeometryPython] BuildingPart001  label="Level"  # Arch/BIM 14 (typed FeaturePython)
  Area = 0
  CompositionType = 0
  Elevation = 0
  GlobalId = 0Y_rRidsD5HgT$XhRHrJ1c
  Group = -> [Group,Group001,Group002]
  Height = 0
  HeightPropagate = true
  IfcData = IfcUID=0Y_rRidsD5HgT$XhRHrJ1c,+2 more (map truncated)
  IfcType = 14
  LevelOffset = 0
  LongName = Level
  MaterialsTable = Undefined=0,1,2,3,4,5,6,7,8,9,10,11,12,13,14,15,16,17,18,19,20,21,22,23,24,25,26,27,28,29,30,31,32,33,34,35,36,37,38,39,40,41,42,4... (+46 chars omitted)
  OnlySolids = true
  expr: Elevation = .Placement.Base.z
FEATURE [App::GeometryPython] BuildingPart  label=" Building"  # Arch/BIM 10 (typed FeaturePython)
  Area = 0
  BuildingType = 39
  CompositionType = 0
  ElevationOfRefHeight = 0
  ElevationOfTerrain = 0
  GlobalId = 2rckVYnYfFABZ6fqlYsD3o
  Group = -> [App__DocumentObjectGroup,BuildingPart001]
  Height = 0
  HeightPropagate = true
  IfcData = IfcUID=2rckVYnYfFABZ6fqlYsD3o,+2 more (map truncated)
  IfcType = 10
  LevelOffset = 0
  LongName = Building
  MaterialsTable = Undefined=0,1,2,3,4,5,6,7,8,9,10,11,12,13,14,15,16,17,18,19,20,21,22,23,24,25,26,27,28,29,30,31,32,33,34,35,36,37,38,39,40,41,42,4... (+46 chars omitted)
  OnlySolids = true
FEATURE [Part::FeaturePython] Site  # Arch/BIM 117 (typed FeaturePython)
  AdditionVolume = 0
  CompositionType = 0
  Declination = 0
  Elevation = 0
  ExtrusionVector = (0,0,-100000)
  GlobalId = 3amnmECn55Rvuueb_50xiu
  Group = -> [BuildingPart]
  IfcData = IfcUID=3amnmECn55Rvuueb_50xiu,+2 more (map truncated)
  IfcType = 117
  Latitude = -2
  LongName = Site
  Longitude = -6
  OriginOffset = (0,0,0)
  Perimeter = 0
  ProjectedArea = 0
  RefElevation = 0
  RemoveSplitter = false
  SubtractionVolume = 0
  TimeZone = 0
  expr: RefElevation = .Elevation.Value
FEATURE [Sketcher::SketchObject] Sketch020
  ArcFitTolerance = 1e-06
  ExternalTypes = [0]
  FullyConstrained = true
  MakeInternals = false
  Placement = pos=(6786.79,20576.5,609.6) rot=(0,0.707107,0.707107;3.14159rad)
  sketch-geometry (24):
    g0: LineSegment StartX=0 StartY=0 StartZ=0 EndX=762 EndY=0 EndZ=0
    g1: LineSegment StartX=762 StartY=0 StartZ=0 EndX=762 EndY=1345 EndZ=0
    g2: LineSegment StartX=762 StartY=1345 StartZ=0 EndX=0 EndY=1345 EndZ=0
    g3: LineSegment StartX=0 StartY=1345 StartZ=0 EndX=0 EndY=0 EndZ=0
    g4: LineSegment StartX=25 StartY=25 StartZ=0 EndX=737 EndY=25 EndZ=0
    g5: LineSegment StartX=737 StartY=25 StartZ=0 EndX=737 EndY=1320 EndZ=0
    g6: LineSegment StartX=737 StartY=1320 StartZ=0 EndX=25 EndY=1320 EndZ=0
    g7: LineSegment StartX=25 StartY=1320 StartZ=0 EndX=25 EndY=25 EndZ=0
    g8: LineSegment StartX=27.5 StartY=27.5 StartZ=0 EndX=734.5 EndY=27.5 EndZ=0
    g9: LineSegment StartX=734.5 StartY=27.5 StartZ=0 EndX=734.5 EndY=671.25 EndZ=0
    g10: LineSegment StartX=734.5 StartY=671.25 StartZ=0 EndX=27.5 EndY=671.25 EndZ=0
    g11: LineSegment StartX=27.5 StartY=671.25 StartZ=0 EndX=27.5 EndY=27.5 EndZ=0
    g12: LineSegment StartX=77.5 StartY=77.5 StartZ=0 EndX=684.5 EndY=77.5 EndZ=0
    g13: LineSegment StartX=684.5 StartY=77.5 StartZ=0 EndX=684.5 EndY=621.25 EndZ=0
    g14: LineSegment StartX=684.5 StartY=621.25 StartZ=0 EndX=77.5 EndY=621.25 EndZ=0
    g15: LineSegment StartX=77.5 StartY=621.25 StartZ=0 EndX=77.5 EndY=77.5 EndZ=0
    g16: LineSegment StartX=27.5 StartY=673.75 StartZ=0 EndX=734.5 EndY=673.75 EndZ=0
    g17: LineSegment StartX=734.5 StartY=673.75 StartZ=0 EndX=734.5 EndY=1317.5 EndZ=0
    g18: LineSegment StartX=734.5 StartY=1317.5 StartZ=0 EndX=27.5 EndY=1317.5 EndZ=0
    g19: LineSegment StartX=27.5 StartY=1317.5 StartZ=0 EndX=27.5 EndY=673.75 EndZ=0
    g20: LineSegment StartX=77.5 StartY=723.75 StartZ=0 EndX=684.5 EndY=723.75 EndZ=0
    g21: LineSegment StartX=684.5 StartY=723.75 StartZ=0 EndX=684.5 EndY=1267.5 EndZ=0
    g22: LineSegment StartX=684.5 StartY=1267.5 StartZ=0 EndX=77.5 EndY=1267.5 EndZ=0
    g23: LineSegment StartX=77.5 StartY=1267.5 StartZ=0 EndX=77.5 EndY=723.75 EndZ=0
  constraints (71):
    c: Coincident(g0,g1)
    c: Coincident(g1,g2)
    c: Coincident(g2,g3)
    c: Coincident(g3,g0)
    c: Horizontal(g0)
    c: Horizontal(g2)
    c: Vertical(g1)
    c: Vertical(g3)
    c: Coincident(g4,g5)
    c: Coincident(g5,g6)
    c: Coincident(g6,g7)
    c: Coincident(g7,g4)
    c: Horizontal(g4)
    c: Horizontal(g6)
    c: Vertical(g5)
    c: Vertical(g7)
    c: DistanceY(g1) = 1345  'Height'
    c: DistanceX(g0) = 762  'Width'
    c: DistanceY(g6,g2) = 25  'Frame1'
    c: DistanceX(g2,g6) = 25  'Frame2'
    c: DistanceX(g4,g0) = 25  'Frame3'
    c: DistanceY(g0,g4) = 25  'Frame4'
    c: Coincident(g0,g-1)
    c: Coincident(g8,g9)
    c: Coincident(g9,g10)
    c: Coincident(g10,g11)
    c: Coincident(g11,g8)
    c: Horizontal(g8)
    c: Horizontal(g10)
    c: Vertical(g9)
    c: Vertical(g11)
    c: Coincident(g12,g13)
    c: Coincident(g13,g14)
    c: Coincident(g14,g15)
    c: Coincident(g15,g12)
    c: Horizontal(g12)
    c: Horizontal(g14)
    c: Vertical(g13)
    c: Vertical(g15)
    c: Coincident(g16,g17)
    c: Coincident(g17,g18)
    c: Coincident(g18,g19)
    c: Coincident(g19,g16)
    c: Horizontal(g16)
    c: Horizontal(g18)
    c: Vertical(g17)
    c: Vertical(g19)
    c: Coincident(g20,g21)
    c: Coincident(g21,g22)
    c: Coincident(g22,g23)
    c: Coincident(g23,g20)
    c: Horizontal(g20)
    c: Horizontal(g22)
    c: Vertical(g21)
    c: Vertical(g23)
    c: DistanceY(g8,g12) = 50
    c: DistanceX(g8,g12) = 50
    c: DistanceX(g21,g17) = 50
    c: DistanceY(g21,g17) = 50
    c: DistanceY(g16,g20) = 50
    c: DistanceY(g10,g14) = -50
    c: Equal(g23,g15)
    c: DistanceX(g12,g20) = 0
    c: DistanceX(g13,g20) = 0
    c: DistanceX(g4,g8) = 2.5
    c: DistanceY(g4,g8) = 2.5
    c: DistanceX(g6,g18) = -2.5
    c: DistanceY(g6,g18) = -2.5
    c: DistanceY(g10,g16) = 2.5
    c: PointOnObject(g9,g17)
    c: PointOnObject(g16,g11)
FEATURE [Part::FeaturePython] Window013  # Arch/BIM 170 (typed FeaturePython)
  Area = 1024890
  Base = -> Sketch020
  Frame = 50.8
  Height = 1345
  HoleDepth = 0
  HoleWire = 0
  HorizontalArea = 0
  Hosts = -> [Wall]
  IfcData = attributes={"GlobalId": {"name": "GlobalId", "type": "IfcGloballyUniqueId", "is_enum": false, "enum_values": []}, "Description": {"... (+1230 chars omitted),+1 more (map truncated)
  IfcType = 170
  LouvreSpacing = 0
  LouvreWidth = 0
  MoveBase = false
  MoveWithHost = true
  Normal = (0,-1,2e-16)
  Opening = 0
  OverallHeight = 1345
  OverallWidth = 762
  PartitioningType = 0
  PerimeterLength = 0
  PredefinedType = 0
  Preset = 4
  SymbolElevation = false
  SymbolPlan = false
  VerticalArea = 0
  Width = 762
  WindowParts = <same value as first occurrence — deduplicated (x10 in doc)>
  expr: OverallHeight = .Height.Value
  expr: OverallWidth = .Width.Value
